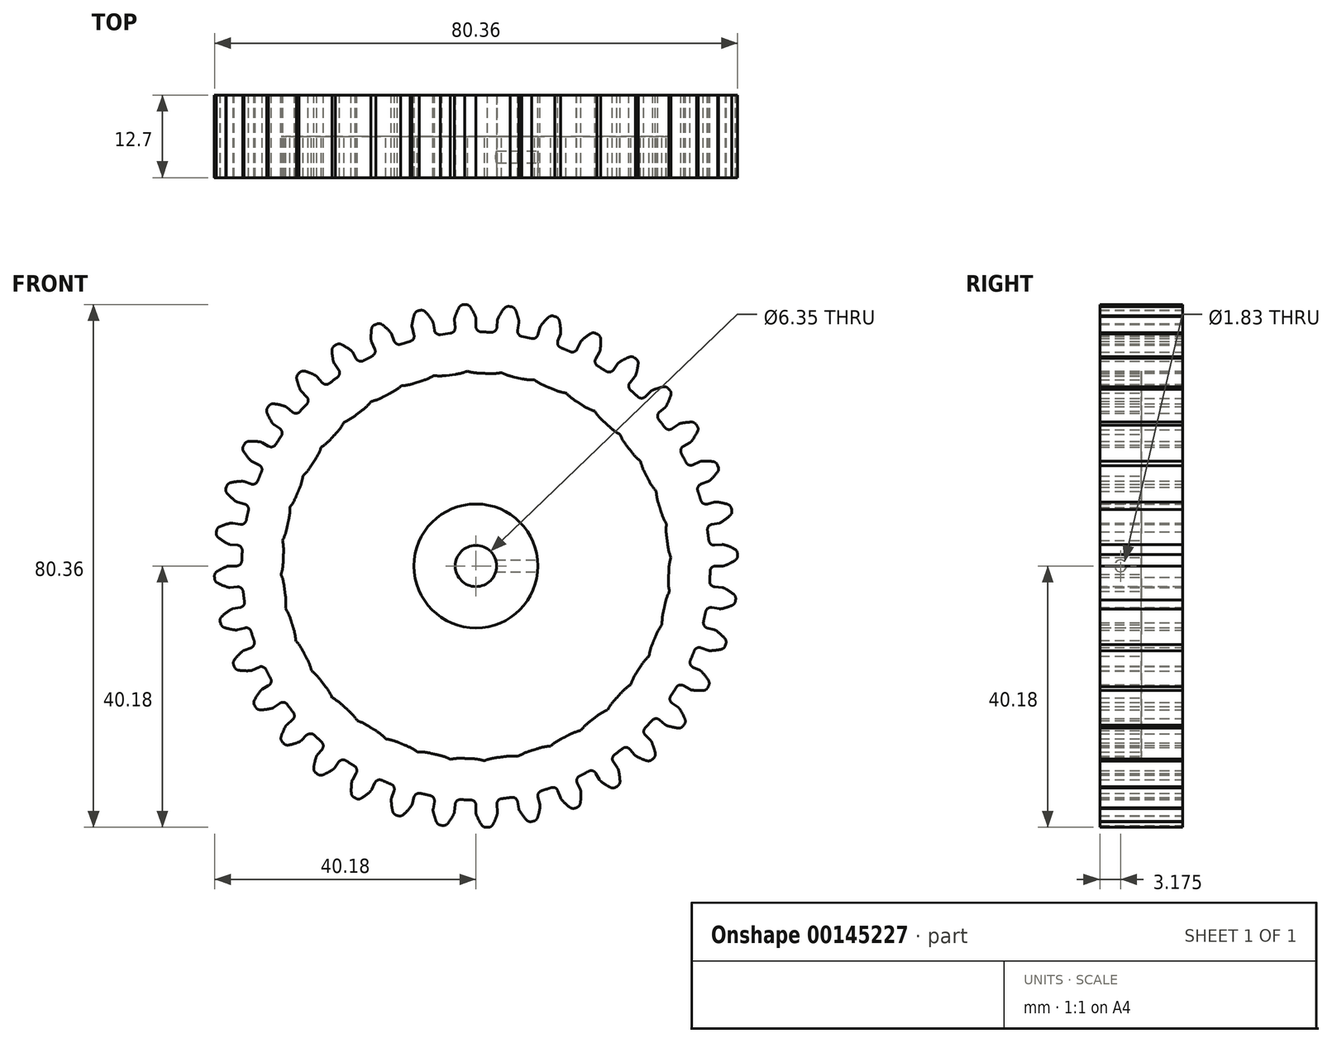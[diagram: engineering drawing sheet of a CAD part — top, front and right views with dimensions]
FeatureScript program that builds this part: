
annotation { "Feature Type Name" : "Feature", "Feature Type Description" : "" }
export const myFeature = defineFeature(function(context is Context, id is Id, definition is map)
    precondition{}
    {
        {
            var Q0;
            Q0=qCreatedBy(makeId("Front.planeOp"),FACE);
            var sketch = newSketch(context, id + "F0", { "sketchPlane" : qUnion([Q0])});
            skArc(sketch, "E0.trimOffspring", {"start": v(-8.9, 34.68) * mm, "mid": v(-8.89, 34.67) * mm, "end": v(-8.88, 34.67) * mm});
            skArc(sketch, "E1.trimOffspring", {"start": v(-0.06, 38.25) * mm, "mid": v(-0.43, 39.05) * mm, "end": v(-0.86, 39.8) * mm});
            skLineSegment(sketch, "E2", {"start": v(-1.59, 40.18) * mm, "end": v(-1.75, 40.18) * mm});
            skLineSegment(sketch, "E3", {"start": v(0, 37.94) * mm, "end": v(0, 36.8) * mm});
            skLineSegment(sketch, "E4.MirrorCS", {"start": v(-1.92, 40.17) * mm, "end": v(-1.75, 40.18) * mm});
            skArc(sketch, "E5.MirrorCS", {"start": v(-3.27, 38.11) * mm, "mid": v(-2.98, 38.94) * mm, "end": v(-2.6, 39.73) * mm});
            skLineSegment(sketch, "E6.MirrorCS", {"start": v(-3.3, 37.8) * mm, "end": v(-3.2, 36.66) * mm});
            skPoint(sketch, "E7.visualSharp", {"position": v(-3.14, 35.85) * mm});
            skArc(sketch, "E7.filletArc", {"start": v(-3.94, 35.77) * mm, "mid": v(-3.4, 36.06) * mm, "end": v(-3.2, 36.66) * mm});
            skPoint(sketch, "E8.visualSharp", {"position": v(0, 35.98) * mm});
            skArc(sketch, "E8.filletArc", {"start": v(0, 36.8) * mm, "mid": v(0.24, 36.22) * mm, "end": v(0.8, 35.97) * mm});
            skPoint(sketch, "E9.visualSharp", {"position": v(-3.32, 37.96) * mm});
            skArc(sketch, "E9.filletArc", {"start": v(-3.27, 38.11) * mm, "mid": v(-3.3, 37.96) * mm, "end": v(-3.3, 37.8) * mm});
            skArc(sketch, "E10.filletArc", {"start": v(0, 37.94) * mm, "mid": v(-0.02, 38.1) * mm, "end": v(-0.06, 38.25) * mm});
            skPoint(sketch, "E11.visualSharp", {"position": v(-2.38, 40.15) * mm});
            skArc(sketch, "E11.filletArc", {"start": v(-1.92, 40.17) * mm, "mid": v(-2.32, 40.04) * mm, "end": v(-2.6, 39.73) * mm});
            skPoint(sketch, "E12.visualSharp", {"position": v(-1.13, 40.2) * mm});
            skArc(sketch, "E12.filletArc", {"start": v(-0.86, 39.8) * mm, "mid": v(-1.18, 40.1) * mm, "end": v(-1.59, 40.18) * mm});
            skArc(sketch, "E13.1.0", {"start": v(-10.1, 34.54) * mm, "mid": v(-9.6, 34.93) * mm, "end": v(-9.52, 35.55) * mm});
            skLineSegment(sketch, "E13.1.1", {"start": v(-9.82, 36.65) * mm, "end": v(-9.52, 35.55) * mm});
            skArc(sketch, "E13.1.2", {"start": v(-9.84, 36.97) * mm, "mid": v(-9.7, 37.83) * mm, "end": v(-9.47, 38.67) * mm});
            skArc(sketch, "E13.1.3", {"start": v(-9.84, 36.97) * mm, "mid": v(-9.85, 36.8) * mm, "end": v(-9.82, 36.65) * mm});
            skArc(sketch, "E13.1.4", {"start": v(-8.87, 39.23) * mm, "mid": v(-9.24, 39.03) * mm, "end": v(-9.47, 38.67) * mm});
            skLineSegment(sketch, "E13.1.5", {"start": v(-8.87, 39.23) * mm, "end": v(-8.7, 39.26) * mm});
            skLineSegment(sketch, "E13.1.6", {"start": v(-8.54, 39.3) * mm, "end": v(-8.7, 39.26) * mm});
            skArc(sketch, "E13.1.7", {"start": v(-7.76, 39.05) * mm, "mid": v(-8.12, 39.28) * mm, "end": v(-8.54, 39.3) * mm});
            skArc(sketch, "E13.1.8", {"start": v(-6.7, 37.66) * mm, "mid": v(-7.2, 38.38) * mm, "end": v(-7.76, 39.05) * mm});
            skArc(sketch, "E13.1.9", {"start": v(-6.59, 37.37) * mm, "mid": v(-6.63, 37.52) * mm, "end": v(-6.7, 37.66) * mm});
            skLineSegment(sketch, "E13.1.10", {"start": v(-6.59, 37.37) * mm, "end": v(-6.4, 36.24) * mm});
            skArc(sketch, "E13.1.11", {"start": v(-6.4, 36.24) * mm, "mid": v(-6.06, 35.71) * mm, "end": v(-5.45, 35.57) * mm});
            skArc(sketch, "E13.2.0", {"start": v(-15.93, 32.26) * mm, "mid": v(-15.52, 32.73) * mm, "end": v(-15.55, 33.35) * mm});
            skLineSegment(sketch, "E13.2.1", {"start": v(-16.04, 34.39) * mm, "end": v(-15.55, 33.35) * mm});
            skArc(sketch, "E13.2.2", {"start": v(-16.11, 34.7) * mm, "mid": v(-16.12, 35.57) * mm, "end": v(-16.04, 36.44) * mm});
            skArc(sketch, "E13.2.3", {"start": v(-16.11, 34.7) * mm, "mid": v(-16.09, 34.54) * mm, "end": v(-16.04, 34.39) * mm});
            skArc(sketch, "E13.2.4", {"start": v(-15.54, 37.1) * mm, "mid": v(-15.88, 36.83) * mm, "end": v(-16.04, 36.44) * mm});
            skLineSegment(sketch, "E13.2.5", {"start": v(-15.54, 37.1) * mm, "end": v(-15.4, 37.16) * mm});
            skLineSegment(sketch, "E13.2.6", {"start": v(-15.24, 37.22) * mm, "end": v(-15.4, 37.16) * mm});
            skArc(sketch, "E13.2.7", {"start": v(-14.43, 37.1) * mm, "mid": v(-14.82, 37.27) * mm, "end": v(-15.24, 37.22) * mm});
            skArc(sketch, "E13.2.8", {"start": v(-13.14, 35.93) * mm, "mid": v(-13.76, 36.55) * mm, "end": v(-14.43, 37.1) * mm});
            skArc(sketch, "E13.2.9", {"start": v(-12.98, 35.65) * mm, "mid": v(-13.05, 35.8) * mm, "end": v(-13.14, 35.93) * mm});
            skLineSegment(sketch, "E13.2.10", {"start": v(-12.98, 35.65) * mm, "end": v(-12.59, 34.58) * mm});
            skArc(sketch, "E13.2.11", {"start": v(-12.59, 34.58) * mm, "mid": v(-12.17, 34.12) * mm, "end": v(-11.55, 34.08) * mm});
            skArc(sketch, "E13.3.0", {"start": v(-21.3, 29) * mm, "mid": v(-20.97, 29.54) * mm, "end": v(-21.1, 30.14) * mm});
            skLineSegment(sketch, "E13.3.1", {"start": v(-21.76, 31.08) * mm, "end": v(-21.1, 30.14) * mm});
            skArc(sketch, "E13.3.2", {"start": v(-21.9, 31.37) * mm, "mid": v(-22.05, 32.23) * mm, "end": v(-22.12, 33.1) * mm});
            skArc(sketch, "E13.3.3", {"start": v(-21.9, 31.37) * mm, "mid": v(-21.84, 31.22) * mm, "end": v(-21.76, 31.08) * mm});
            skArc(sketch, "E13.3.4", {"start": v(-21.75, 33.83) * mm, "mid": v(-22.03, 33.51) * mm, "end": v(-22.12, 33.1) * mm});
            skLineSegment(sketch, "E13.3.5", {"start": v(-21.75, 33.83) * mm, "end": v(-21.6, 33.92) * mm});
            skLineSegment(sketch, "E13.3.6", {"start": v(-21.47, 34) * mm, "end": v(-21.6, 33.92) * mm});
            skArc(sketch, "E13.3.7", {"start": v(-20.65, 34.04) * mm, "mid": v(-21.06, 34.13) * mm, "end": v(-21.47, 34) * mm});
            skArc(sketch, "E13.3.8", {"start": v(-19.18, 33.1) * mm, "mid": v(-19.9, 33.6) * mm, "end": v(-20.65, 34.04) * mm});
            skArc(sketch, "E13.3.9", {"start": v(-18.97, 32.86) * mm, "mid": v(-19.06, 32.99) * mm, "end": v(-19.18, 33.1) * mm});
            skLineSegment(sketch, "E13.3.10", {"start": v(-18.97, 32.86) * mm, "end": v(-18.4, 31.87) * mm});
            skArc(sketch, "E13.3.11", {"start": v(-18.4, 31.87) * mm, "mid": v(-17.9, 31.49) * mm, "end": v(-17.29, 31.56) * mm});
            skArc(sketch, "E13.4.0", {"start": v(-26, 24.87) * mm, "mid": v(-25.78, 25.45) * mm, "end": v(-26.02, 26.02) * mm});
            skLineSegment(sketch, "E13.4.1", {"start": v(-26.83, 26.83) * mm, "end": v(-26.02, 26.02) * mm});
            skArc(sketch, "E13.4.2", {"start": v(-27, 27.1) * mm, "mid": v(-27.3, 27.91) * mm, "end": v(-27.53, 28.76) * mm});
            skArc(sketch, "E13.4.3", {"start": v(-27, 27.1) * mm, "mid": v(-26.93, 26.95) * mm, "end": v(-26.83, 26.83) * mm});
            skArc(sketch, "E13.4.4", {"start": v(-27.3, 29.54) * mm, "mid": v(-27.52, 29.18) * mm, "end": v(-27.53, 28.76) * mm});
            skLineSegment(sketch, "E13.4.5", {"start": v(-27.3, 29.54) * mm, "end": v(-27.17, 29.65) * mm});
            skLineSegment(sketch, "E13.4.6", {"start": v(-27.05, 29.76) * mm, "end": v(-27.17, 29.65) * mm});
            skArc(sketch, "E13.4.7", {"start": v(-26.25, 29.94) * mm, "mid": v(-26.67, 29.95) * mm, "end": v(-27.05, 29.76) * mm});
            skArc(sketch, "E13.4.8", {"start": v(-24.64, 29.26) * mm, "mid": v(-25.43, 29.64) * mm, "end": v(-26.25, 29.94) * mm});
            skArc(sketch, "E13.4.9", {"start": v(-24.39, 29.07) * mm, "mid": v(-24.5, 29.18) * mm, "end": v(-24.64, 29.26) * mm});
            skLineSegment(sketch, "E13.4.10", {"start": v(-24.39, 29.07) * mm, "end": v(-23.65, 28.19) * mm});
            skArc(sketch, "E13.4.11", {"start": v(-23.65, 28.19) * mm, "mid": v(-23.1, 27.9) * mm, "end": v(-22.5, 28.08) * mm});
            skArc(sketch, "E13.5.0", {"start": v(-29.93, 19.97) * mm, "mid": v(-29.8, 20.58) * mm, "end": v(-30.14, 21.1) * mm});
            skLineSegment(sketch, "E13.5.1", {"start": v(-31.08, 21.76) * mm, "end": v(-30.14, 21.1) * mm});
            skArc(sketch, "E13.5.2", {"start": v(-31.3, 22) * mm, "mid": v(-31.74, 22.75) * mm, "end": v(-32.11, 23.54) * mm});
            skArc(sketch, "E13.5.3", {"start": v(-31.3, 22) * mm, "mid": v(-31.2, 21.87) * mm, "end": v(-31.08, 21.76) * mm});
            skArc(sketch, "E13.5.4", {"start": v(-32, 24.35) * mm, "mid": v(-32.17, 23.96) * mm, "end": v(-32.11, 23.54) * mm});
            skLineSegment(sketch, "E13.5.5", {"start": v(-32, 24.35) * mm, "end": v(-31.9, 24.48) * mm});
            skLineSegment(sketch, "E13.5.6", {"start": v(-31.8, 24.61) * mm, "end": v(-31.9, 24.48) * mm});
            skArc(sketch, "E13.5.7", {"start": v(-31.05, 24.92) * mm, "mid": v(-31.47, 24.87) * mm, "end": v(-31.8, 24.61) * mm});
            skArc(sketch, "E13.5.8", {"start": v(-29.34, 24.54) * mm, "mid": v(-30.19, 24.77) * mm, "end": v(-31.05, 24.92) * mm});
            skArc(sketch, "E13.5.9", {"start": v(-29.07, 24.39) * mm, "mid": v(-29.2, 24.48) * mm, "end": v(-29.34, 24.54) * mm});
            skLineSegment(sketch, "E13.5.10", {"start": v(-29.07, 24.39) * mm, "end": v(-28.19, 23.65) * mm});
            skArc(sketch, "E13.5.11", {"start": v(-28.19, 23.65) * mm, "mid": v(-27.6, 23.46) * mm, "end": v(-27.04, 23.74) * mm});
            skArc(sketch, "E13.6.0", {"start": v(-32.94, 14.47) * mm, "mid": v(-32.93, 15.1) * mm, "end": v(-33.35, 15.55) * mm});
            skLineSegment(sketch, "E13.6.1", {"start": v(-34.39, 16.04) * mm, "end": v(-33.35, 15.55) * mm});
            skArc(sketch, "E13.6.2", {"start": v(-34.64, 16.22) * mm, "mid": v(-35.2, 16.89) * mm, "end": v(-35.7, 17.6) * mm});
            skArc(sketch, "E13.6.3", {"start": v(-34.64, 16.22) * mm, "mid": v(-34.52, 16.12) * mm, "end": v(-34.39, 16.04) * mm});
            skArc(sketch, "E13.6.4", {"start": v(-35.75, 18.42) * mm, "mid": v(-35.84, 18) * mm, "end": v(-35.7, 17.6) * mm});
            skLineSegment(sketch, "E13.6.5", {"start": v(-35.75, 18.42) * mm, "end": v(-35.67, 18.57) * mm});
            skLineSegment(sketch, "E13.6.6", {"start": v(-35.6, 18.72) * mm, "end": v(-35.67, 18.57) * mm});
            skArc(sketch, "E13.6.7", {"start": v(-34.9, 19.15) * mm, "mid": v(-35.3, 19.03) * mm, "end": v(-35.6, 18.72) * mm});
            skArc(sketch, "E13.6.8", {"start": v(-33.16, 19.07) * mm, "mid": v(-34.03, 19.15) * mm, "end": v(-34.9, 19.15) * mm});
            skArc(sketch, "E13.6.9", {"start": v(-32.86, 18.97) * mm, "mid": v(-33, 19.04) * mm, "end": v(-33.16, 19.07) * mm});
            skLineSegment(sketch, "E13.6.10", {"start": v(-32.86, 18.97) * mm, "end": v(-31.87, 18.4) * mm});
            skArc(sketch, "E13.6.11", {"start": v(-31.87, 18.4) * mm, "mid": v(-31.25, 18.31) * mm, "end": v(-30.75, 18.69) * mm});
            skArc(sketch, "E13.7.0", {"start": v(-34.96, 8.53) * mm, "mid": v(-35.05, 9.15) * mm, "end": v(-35.55, 9.52) * mm});
            skLineSegment(sketch, "E13.7.1", {"start": v(-36.65, 9.82) * mm, "end": v(-35.55, 9.52) * mm});
            skArc(sketch, "E13.7.2", {"start": v(-36.93, 9.96) * mm, "mid": v(-37.6, 10.52) * mm, "end": v(-38.22, 11.14) * mm});
            skArc(sketch, "E13.7.3", {"start": v(-36.93, 9.96) * mm, "mid": v(-36.8, 9.88) * mm, "end": v(-36.65, 9.82) * mm});
            skArc(sketch, "E13.7.4", {"start": v(-38.4, 11.94) * mm, "mid": v(-38.42, 11.51) * mm, "end": v(-38.22, 11.14) * mm});
            skLineSegment(sketch, "E13.7.5", {"start": v(-38.4, 11.94) * mm, "end": v(-38.36, 12.1) * mm});
            skLineSegment(sketch, "E13.7.6", {"start": v(-38.3, 12.25) * mm, "end": v(-38.36, 12.1) * mm});
            skArc(sketch, "E13.7.7", {"start": v(-37.7, 12.8) * mm, "mid": v(-38.08, 12.6) * mm, "end": v(-38.3, 12.25) * mm});
            skArc(sketch, "E13.7.8", {"start": v(-35.97, 13.03) * mm, "mid": v(-36.84, 12.95) * mm, "end": v(-37.7, 12.8) * mm});
            skArc(sketch, "E13.7.9", {"start": v(-35.65, 12.98) * mm, "mid": v(-35.8, 13.02) * mm, "end": v(-35.97, 13.03) * mm});
            skLineSegment(sketch, "E13.7.10", {"start": v(-35.65, 12.98) * mm, "end": v(-34.58, 12.59) * mm});
            skArc(sketch, "E13.7.11", {"start": v(-34.58, 12.59) * mm, "mid": v(-33.96, 12.6) * mm, "end": v(-33.53, 13.06) * mm});
            skArc(sketch, "E13.8.0", {"start": v(-35.9, 2.33) * mm, "mid": v(-36.1, 2.92) * mm, "end": v(-36.66, 3.2) * mm});
            skLineSegment(sketch, "E13.8.1", {"start": v(-37.8, 3.3) * mm, "end": v(-36.66, 3.2) * mm});
            skArc(sketch, "E13.8.2", {"start": v(-38.1, 3.4) * mm, "mid": v(-38.86, 3.83) * mm, "end": v(-39.58, 4.33) * mm});
            skArc(sketch, "E13.8.3", {"start": v(-38.1, 3.4) * mm, "mid": v(-37.95, 3.34) * mm, "end": v(-37.8, 3.3) * mm});
            skArc(sketch, "E13.8.4", {"start": v(-39.9, 5.09) * mm, "mid": v(-39.84, 4.67) * mm, "end": v(-39.58, 4.33) * mm});
            skLineSegment(sketch, "E13.8.5", {"start": v(-39.9, 5.09) * mm, "end": v(-39.87, 5.25) * mm});
            skLineSegment(sketch, "E13.8.6", {"start": v(-39.85, 5.41) * mm, "end": v(-39.87, 5.25) * mm});
            skArc(sketch, "E13.8.7", {"start": v(-39.35, 6.06) * mm, "mid": v(-39.69, 5.8) * mm, "end": v(-39.85, 5.41) * mm});
            skArc(sketch, "E13.8.8", {"start": v(-37.68, 6.58) * mm, "mid": v(-38.53, 6.36) * mm, "end": v(-39.35, 6.06) * mm});
            skArc(sketch, "E13.8.9", {"start": v(-37.37, 6.59) * mm, "mid": v(-37.52, 6.6) * mm, "end": v(-37.68, 6.58) * mm});
            skLineSegment(sketch, "E13.8.10", {"start": v(-37.37, 6.59) * mm, "end": v(-36.24, 6.4) * mm});
            skArc(sketch, "E13.8.11", {"start": v(-36.24, 6.4) * mm, "mid": v(-35.63, 6.52) * mm, "end": v(-35.29, 7.04) * mm});
            skArc(sketch, "E13.9.0", {"start": v(-35.77, -3.94) * mm, "mid": v(-36.06, -3.4) * mm, "end": v(-36.66, -3.2) * mm});
            skLineSegment(sketch, "E13.9.1", {"start": v(-37.8, -3.3) * mm, "end": v(-36.66, -3.2) * mm});
            skArc(sketch, "E13.9.2", {"start": v(-38.11, -3.27) * mm, "mid": v(-38.94, -2.98) * mm, "end": v(-39.73, -2.6) * mm});
            skArc(sketch, "E13.9.3", {"start": v(-38.11, -3.27) * mm, "mid": v(-37.96, -3.3) * mm, "end": v(-37.8, -3.3) * mm});
            skArc(sketch, "E13.9.4", {"start": v(-40.17, -1.92) * mm, "mid": v(-40.04, -2.32) * mm, "end": v(-39.73, -2.6) * mm});
            skLineSegment(sketch, "E13.9.5", {"start": v(-40.17, -1.92) * mm, "end": v(-40.18, -1.75) * mm});
            skLineSegment(sketch, "E13.9.6", {"start": v(-40.18, -1.59) * mm, "end": v(-40.18, -1.75) * mm});
            skArc(sketch, "E13.9.7", {"start": v(-39.8, -0.86) * mm, "mid": v(-40.1, -1.18) * mm, "end": v(-40.18, -1.59) * mm});
            skArc(sketch, "E13.9.8", {"start": v(-38.25, -0.06) * mm, "mid": v(-39.05, -0.43) * mm, "end": v(-39.8, -0.86) * mm});
            skArc(sketch, "E13.9.9", {"start": v(-37.94, 0) * mm, "mid": v(-38.1, -0.02) * mm, "end": v(-38.25, -0.06) * mm});
            skLineSegment(sketch, "E13.9.10", {"start": v(-37.94, 0) * mm, "end": v(-36.8, 0) * mm});
            skArc(sketch, "E13.9.11", {"start": v(-36.8, 0) * mm, "mid": v(-36.22, 0.24) * mm, "end": v(-35.97, 0.8) * mm});
            skArc(sketch, "E13.10.0", {"start": v(-34.54, -10.1) * mm, "mid": v(-34.93, -9.6) * mm, "end": v(-35.55, -9.52) * mm});
            skLineSegment(sketch, "E13.10.1", {"start": v(-36.65, -9.82) * mm, "end": v(-35.55, -9.52) * mm});
            skArc(sketch, "E13.10.2", {"start": v(-36.97, -9.84) * mm, "mid": v(-37.83, -9.7) * mm, "end": v(-38.67, -9.47) * mm});
            skArc(sketch, "E13.10.3", {"start": v(-36.97, -9.84) * mm, "mid": v(-36.8, -9.85) * mm, "end": v(-36.65, -9.82) * mm});
            skArc(sketch, "E13.10.4", {"start": v(-39.23, -8.87) * mm, "mid": v(-39.03, -9.24) * mm, "end": v(-38.67, -9.47) * mm});
            skLineSegment(sketch, "E13.10.5", {"start": v(-39.23, -8.87) * mm, "end": v(-39.26, -8.7) * mm});
            skLineSegment(sketch, "E13.10.6", {"start": v(-39.3, -8.54) * mm, "end": v(-39.26, -8.7) * mm});
            skArc(sketch, "E13.10.7", {"start": v(-39.05, -7.76) * mm, "mid": v(-39.28, -8.12) * mm, "end": v(-39.3, -8.54) * mm});
            skArc(sketch, "E13.10.8", {"start": v(-37.66, -6.7) * mm, "mid": v(-38.38, -7.2) * mm, "end": v(-39.05, -7.76) * mm});
            skArc(sketch, "E13.10.9", {"start": v(-37.37, -6.59) * mm, "mid": v(-37.52, -6.63) * mm, "end": v(-37.66, -6.7) * mm});
            skLineSegment(sketch, "E13.10.10", {"start": v(-37.37, -6.59) * mm, "end": v(-36.24, -6.4) * mm});
            skArc(sketch, "E13.10.11", {"start": v(-36.24, -6.4) * mm, "mid": v(-35.71, -6.06) * mm, "end": v(-35.57, -5.45) * mm});
            skArc(sketch, "E13.11.0", {"start": v(-32.26, -15.93) * mm, "mid": v(-32.73, -15.52) * mm, "end": v(-33.35, -15.55) * mm});
            skLineSegment(sketch, "E13.11.1", {"start": v(-34.39, -16.04) * mm, "end": v(-33.35, -15.55) * mm});
            skArc(sketch, "E13.11.2", {"start": v(-34.7, -16.11) * mm, "mid": v(-35.57, -16.12) * mm, "end": v(-36.44, -16.04) * mm});
            skArc(sketch, "E13.11.3", {"start": v(-34.7, -16.11) * mm, "mid": v(-34.54, -16.09) * mm, "end": v(-34.39, -16.04) * mm});
            skArc(sketch, "E13.11.4", {"start": v(-37.1, -15.54) * mm, "mid": v(-36.83, -15.88) * mm, "end": v(-36.44, -16.04) * mm});
            skLineSegment(sketch, "E13.11.5", {"start": v(-37.1, -15.54) * mm, "end": v(-37.16, -15.4) * mm});
            skLineSegment(sketch, "E13.11.6", {"start": v(-37.22, -15.24) * mm, "end": v(-37.16, -15.4) * mm});
            skArc(sketch, "E13.11.7", {"start": v(-37.1, -14.43) * mm, "mid": v(-37.27, -14.82) * mm, "end": v(-37.22, -15.24) * mm});
            skArc(sketch, "E13.11.8", {"start": v(-35.93, -13.14) * mm, "mid": v(-36.55, -13.76) * mm, "end": v(-37.1, -14.43) * mm});
            skArc(sketch, "E13.11.9", {"start": v(-35.65, -12.98) * mm, "mid": v(-35.8, -13.05) * mm, "end": v(-35.93, -13.14) * mm});
            skLineSegment(sketch, "E13.11.10", {"start": v(-35.65, -12.98) * mm, "end": v(-34.58, -12.59) * mm});
            skArc(sketch, "E13.11.11", {"start": v(-34.58, -12.59) * mm, "mid": v(-34.12, -12.17) * mm, "end": v(-34.08, -11.55) * mm});
            skArc(sketch, "E13.12.0", {"start": v(-29, -21.3) * mm, "mid": v(-29.54, -20.97) * mm, "end": v(-30.14, -21.1) * mm});
            skLineSegment(sketch, "E13.12.1", {"start": v(-31.08, -21.76) * mm, "end": v(-30.14, -21.1) * mm});
            skArc(sketch, "E13.12.2", {"start": v(-31.37, -21.9) * mm, "mid": v(-32.23, -22.05) * mm, "end": v(-33.1, -22.12) * mm});
            skArc(sketch, "E13.12.3", {"start": v(-31.37, -21.9) * mm, "mid": v(-31.22, -21.84) * mm, "end": v(-31.08, -21.76) * mm});
            skArc(sketch, "E13.12.4", {"start": v(-33.83, -21.75) * mm, "mid": v(-33.51, -22.03) * mm, "end": v(-33.1, -22.12) * mm});
            skLineSegment(sketch, "E13.12.5", {"start": v(-33.83, -21.75) * mm, "end": v(-33.92, -21.6) * mm});
            skLineSegment(sketch, "E13.12.6", {"start": v(-34, -21.47) * mm, "end": v(-33.92, -21.6) * mm});
            skArc(sketch, "E13.12.7", {"start": v(-34.04, -20.65) * mm, "mid": v(-34.13, -21.06) * mm, "end": v(-34, -21.47) * mm});
            skArc(sketch, "E13.12.8", {"start": v(-33.1, -19.18) * mm, "mid": v(-33.6, -19.9) * mm, "end": v(-34.04, -20.65) * mm});
            skArc(sketch, "E13.12.9", {"start": v(-32.86, -18.97) * mm, "mid": v(-32.99, -19.06) * mm, "end": v(-33.1, -19.18) * mm});
            skLineSegment(sketch, "E13.12.10", {"start": v(-32.86, -18.97) * mm, "end": v(-31.87, -18.4) * mm});
            skArc(sketch, "E13.12.11", {"start": v(-31.87, -18.4) * mm, "mid": v(-31.49, -17.9) * mm, "end": v(-31.56, -17.29) * mm});
            skArc(sketch, "E13.13.0", {"start": v(-24.87, -26) * mm, "mid": v(-25.45, -25.78) * mm, "end": v(-26.02, -26.02) * mm});
            skLineSegment(sketch, "E13.13.1", {"start": v(-26.83, -26.83) * mm, "end": v(-26.02, -26.02) * mm});
            skArc(sketch, "E13.13.2", {"start": v(-27.1, -27) * mm, "mid": v(-27.91, -27.3) * mm, "end": v(-28.76, -27.53) * mm});
            skArc(sketch, "E13.13.3", {"start": v(-27.1, -27) * mm, "mid": v(-26.95, -26.93) * mm, "end": v(-26.83, -26.83) * mm});
            skArc(sketch, "E13.13.4", {"start": v(-29.54, -27.3) * mm, "mid": v(-29.18, -27.52) * mm, "end": v(-28.76, -27.53) * mm});
            skLineSegment(sketch, "E13.13.5", {"start": v(-29.54, -27.3) * mm, "end": v(-29.65, -27.17) * mm});
            skLineSegment(sketch, "E13.13.6", {"start": v(-29.76, -27.05) * mm, "end": v(-29.65, -27.17) * mm});
            skArc(sketch, "E13.13.7", {"start": v(-29.94, -26.25) * mm, "mid": v(-29.95, -26.67) * mm, "end": v(-29.76, -27.05) * mm});
            skArc(sketch, "E13.13.8", {"start": v(-29.26, -24.64) * mm, "mid": v(-29.64, -25.43) * mm, "end": v(-29.94, -26.25) * mm});
            skArc(sketch, "E13.13.9", {"start": v(-29.07, -24.39) * mm, "mid": v(-29.18, -24.5) * mm, "end": v(-29.26, -24.64) * mm});
            skLineSegment(sketch, "E13.13.10", {"start": v(-29.07, -24.39) * mm, "end": v(-28.19, -23.65) * mm});
            skArc(sketch, "E13.13.11", {"start": v(-28.19, -23.65) * mm, "mid": v(-27.9, -23.1) * mm, "end": v(-28.08, -22.5) * mm});
            skArc(sketch, "E13.14.0", {"start": v(-19.97, -29.93) * mm, "mid": v(-20.58, -29.8) * mm, "end": v(-21.1, -30.14) * mm});
            skLineSegment(sketch, "E13.14.1", {"start": v(-21.76, -31.08) * mm, "end": v(-21.1, -30.14) * mm});
            skArc(sketch, "E13.14.2", {"start": v(-22, -31.3) * mm, "mid": v(-22.75, -31.74) * mm, "end": v(-23.54, -32.11) * mm});
            skArc(sketch, "E13.14.3", {"start": v(-22, -31.3) * mm, "mid": v(-21.87, -31.2) * mm, "end": v(-21.76, -31.08) * mm});
            skArc(sketch, "E13.14.4", {"start": v(-24.35, -32) * mm, "mid": v(-23.96, -32.17) * mm, "end": v(-23.54, -32.11) * mm});
            skLineSegment(sketch, "E13.14.5", {"start": v(-24.35, -32) * mm, "end": v(-24.48, -31.9) * mm});
            skLineSegment(sketch, "E13.14.6", {"start": v(-24.61, -31.8) * mm, "end": v(-24.48, -31.9) * mm});
            skArc(sketch, "E13.14.7", {"start": v(-24.92, -31.05) * mm, "mid": v(-24.87, -31.47) * mm, "end": v(-24.61, -31.8) * mm});
            skArc(sketch, "E13.14.8", {"start": v(-24.54, -29.34) * mm, "mid": v(-24.77, -30.19) * mm, "end": v(-24.92, -31.05) * mm});
            skArc(sketch, "E13.14.9", {"start": v(-24.39, -29.07) * mm, "mid": v(-24.48, -29.2) * mm, "end": v(-24.54, -29.34) * mm});
            skLineSegment(sketch, "E13.14.10", {"start": v(-24.39, -29.07) * mm, "end": v(-23.65, -28.19) * mm});
            skArc(sketch, "E13.14.11", {"start": v(-23.65, -28.19) * mm, "mid": v(-23.46, -27.6) * mm, "end": v(-23.74, -27.04) * mm});
            skArc(sketch, "E13.15.0", {"start": v(-14.47, -32.94) * mm, "mid": v(-15.1, -32.93) * mm, "end": v(-15.55, -33.35) * mm});
            skLineSegment(sketch, "E13.15.1", {"start": v(-16.04, -34.39) * mm, "end": v(-15.55, -33.35) * mm});
            skArc(sketch, "E13.15.2", {"start": v(-16.22, -34.64) * mm, "mid": v(-16.89, -35.2) * mm, "end": v(-17.6, -35.7) * mm});
            skArc(sketch, "E13.15.3", {"start": v(-16.22, -34.64) * mm, "mid": v(-16.12, -34.52) * mm, "end": v(-16.04, -34.39) * mm});
            skArc(sketch, "E13.15.4", {"start": v(-18.42, -35.75) * mm, "mid": v(-18, -35.84) * mm, "end": v(-17.6, -35.7) * mm});
            skLineSegment(sketch, "E13.15.5", {"start": v(-18.42, -35.75) * mm, "end": v(-18.57, -35.67) * mm});
            skLineSegment(sketch, "E13.15.6", {"start": v(-18.72, -35.6) * mm, "end": v(-18.57, -35.67) * mm});
            skArc(sketch, "E13.15.7", {"start": v(-19.15, -34.9) * mm, "mid": v(-19.03, -35.3) * mm, "end": v(-18.72, -35.6) * mm});
            skArc(sketch, "E13.15.8", {"start": v(-19.07, -33.16) * mm, "mid": v(-19.15, -34.03) * mm, "end": v(-19.15, -34.9) * mm});
            skArc(sketch, "E13.15.9", {"start": v(-18.97, -32.86) * mm, "mid": v(-19.04, -33) * mm, "end": v(-19.07, -33.16) * mm});
            skLineSegment(sketch, "E13.15.10", {"start": v(-18.97, -32.86) * mm, "end": v(-18.4, -31.87) * mm});
            skArc(sketch, "E13.15.11", {"start": v(-18.4, -31.87) * mm, "mid": v(-18.31, -31.25) * mm, "end": v(-18.69, -30.75) * mm});
            skArc(sketch, "E13.16.0", {"start": v(-8.53, -34.96) * mm, "mid": v(-9.15, -35.05) * mm, "end": v(-9.52, -35.55) * mm});
            skLineSegment(sketch, "E13.16.1", {"start": v(-9.82, -36.65) * mm, "end": v(-9.52, -35.55) * mm});
            skArc(sketch, "E13.16.2", {"start": v(-9.96, -36.93) * mm, "mid": v(-10.52, -37.6) * mm, "end": v(-11.14, -38.22) * mm});
            skArc(sketch, "E13.16.3", {"start": v(-9.96, -36.93) * mm, "mid": v(-9.88, -36.8) * mm, "end": v(-9.82, -36.65) * mm});
            skArc(sketch, "E13.16.4", {"start": v(-11.94, -38.4) * mm, "mid": v(-11.51, -38.42) * mm, "end": v(-11.14, -38.22) * mm});
            skLineSegment(sketch, "E13.16.5", {"start": v(-11.94, -38.4) * mm, "end": v(-12.1, -38.36) * mm});
            skLineSegment(sketch, "E13.16.6", {"start": v(-12.25, -38.3) * mm, "end": v(-12.1, -38.36) * mm});
            skArc(sketch, "E13.16.7", {"start": v(-12.8, -37.7) * mm, "mid": v(-12.6, -38.08) * mm, "end": v(-12.25, -38.3) * mm});
            skArc(sketch, "E13.16.8", {"start": v(-13.03, -35.97) * mm, "mid": v(-12.95, -36.84) * mm, "end": v(-12.8, -37.7) * mm});
            skArc(sketch, "E13.16.9", {"start": v(-12.98, -35.65) * mm, "mid": v(-13.02, -35.8) * mm, "end": v(-13.03, -35.97) * mm});
            skLineSegment(sketch, "E13.16.10", {"start": v(-12.98, -35.65) * mm, "end": v(-12.59, -34.58) * mm});
            skArc(sketch, "E13.16.11", {"start": v(-12.59, -34.58) * mm, "mid": v(-12.6, -33.96) * mm, "end": v(-13.06, -33.53) * mm});
            skArc(sketch, "E13.17.0", {"start": v(-2.33, -35.9) * mm, "mid": v(-2.92, -36.1) * mm, "end": v(-3.2, -36.66) * mm});
            skLineSegment(sketch, "E13.17.1", {"start": v(-3.3, -37.8) * mm, "end": v(-3.2, -36.66) * mm});
            skArc(sketch, "E13.17.2", {"start": v(-3.4, -38.1) * mm, "mid": v(-3.83, -38.86) * mm, "end": v(-4.33, -39.58) * mm});
            skArc(sketch, "E13.17.3", {"start": v(-3.4, -38.1) * mm, "mid": v(-3.34, -37.95) * mm, "end": v(-3.3, -37.8) * mm});
            skArc(sketch, "E13.17.4", {"start": v(-5.09, -39.9) * mm, "mid": v(-4.67, -39.84) * mm, "end": v(-4.33, -39.58) * mm});
            skLineSegment(sketch, "E13.17.5", {"start": v(-5.09, -39.9) * mm, "end": v(-5.25, -39.87) * mm});
            skLineSegment(sketch, "E13.17.6", {"start": v(-5.41, -39.85) * mm, "end": v(-5.25, -39.87) * mm});
            skArc(sketch, "E13.17.7", {"start": v(-6.06, -39.35) * mm, "mid": v(-5.8, -39.69) * mm, "end": v(-5.41, -39.85) * mm});
            skArc(sketch, "E13.17.8", {"start": v(-6.58, -37.68) * mm, "mid": v(-6.36, -38.53) * mm, "end": v(-6.06, -39.35) * mm});
            skArc(sketch, "E13.17.9", {"start": v(-6.59, -37.37) * mm, "mid": v(-6.6, -37.52) * mm, "end": v(-6.58, -37.68) * mm});
            skLineSegment(sketch, "E13.17.10", {"start": v(-6.59, -37.37) * mm, "end": v(-6.4, -36.24) * mm});
            skArc(sketch, "E13.17.11", {"start": v(-6.4, -36.24) * mm, "mid": v(-6.52, -35.63) * mm, "end": v(-7.04, -35.29) * mm});
            skArc(sketch, "E13.18.0", {"start": v(3.94, -35.77) * mm, "mid": v(3.4, -36.06) * mm, "end": v(3.2, -36.66) * mm});
            skLineSegment(sketch, "E13.18.1", {"start": v(3.3, -37.8) * mm, "end": v(3.2, -36.66) * mm});
            skArc(sketch, "E13.18.2", {"start": v(3.27, -38.11) * mm, "mid": v(2.98, -38.94) * mm, "end": v(2.6, -39.73) * mm});
            skArc(sketch, "E13.18.3", {"start": v(3.27, -38.11) * mm, "mid": v(3.3, -37.96) * mm, "end": v(3.3, -37.8) * mm});
            skArc(sketch, "E13.18.4", {"start": v(1.92, -40.17) * mm, "mid": v(2.32, -40.04) * mm, "end": v(2.6, -39.73) * mm});
            skLineSegment(sketch, "E13.18.5", {"start": v(1.92, -40.17) * mm, "end": v(1.75, -40.18) * mm});
            skLineSegment(sketch, "E13.18.6", {"start": v(1.59, -40.18) * mm, "end": v(1.75, -40.18) * mm});
            skArc(sketch, "E13.18.7", {"start": v(0.86, -39.8) * mm, "mid": v(1.18, -40.1) * mm, "end": v(1.59, -40.18) * mm});
            skArc(sketch, "E13.18.8", {"start": v(0.06, -38.25) * mm, "mid": v(0.43, -39.05) * mm, "end": v(0.86, -39.8) * mm});
            skArc(sketch, "E13.18.9", {"start": v(0, -37.94) * mm, "mid": v(0.02, -38.1) * mm, "end": v(0.06, -38.25) * mm});
            skLineSegment(sketch, "E13.18.10", {"start": v(0, -37.94) * mm, "end": v(0, -36.8) * mm});
            skArc(sketch, "E13.18.11", {"start": v(0, -36.8) * mm, "mid": v(-0.24, -36.22) * mm, "end": v(-0.8, -35.97) * mm});
            skArc(sketch, "E13.19.0", {"start": v(10.1, -34.54) * mm, "mid": v(9.6, -34.93) * mm, "end": v(9.52, -35.55) * mm});
            skLineSegment(sketch, "E13.19.1", {"start": v(9.82, -36.65) * mm, "end": v(9.52, -35.55) * mm});
            skArc(sketch, "E13.19.2", {"start": v(9.84, -36.97) * mm, "mid": v(9.7, -37.83) * mm, "end": v(9.47, -38.67) * mm});
            skArc(sketch, "E13.19.3", {"start": v(9.84, -36.97) * mm, "mid": v(9.85, -36.8) * mm, "end": v(9.82, -36.65) * mm});
            skArc(sketch, "E13.19.4", {"start": v(8.87, -39.23) * mm, "mid": v(9.24, -39.03) * mm, "end": v(9.47, -38.67) * mm});
            skLineSegment(sketch, "E13.19.5", {"start": v(8.87, -39.23) * mm, "end": v(8.7, -39.26) * mm});
            skLineSegment(sketch, "E13.19.6", {"start": v(8.54, -39.3) * mm, "end": v(8.7, -39.26) * mm});
            skArc(sketch, "E13.19.7", {"start": v(7.76, -39.05) * mm, "mid": v(8.12, -39.28) * mm, "end": v(8.54, -39.3) * mm});
            skArc(sketch, "E13.19.8", {"start": v(6.7, -37.66) * mm, "mid": v(7.2, -38.38) * mm, "end": v(7.76, -39.05) * mm});
            skArc(sketch, "E13.19.9", {"start": v(6.59, -37.37) * mm, "mid": v(6.63, -37.52) * mm, "end": v(6.7, -37.66) * mm});
            skLineSegment(sketch, "E13.19.10", {"start": v(6.59, -37.37) * mm, "end": v(6.4, -36.24) * mm});
            skArc(sketch, "E13.19.11", {"start": v(6.4, -36.24) * mm, "mid": v(6.06, -35.71) * mm, "end": v(5.45, -35.57) * mm});
            skArc(sketch, "E13.20.0", {"start": v(15.93, -32.26) * mm, "mid": v(15.52, -32.73) * mm, "end": v(15.55, -33.35) * mm});
            skLineSegment(sketch, "E13.20.1", {"start": v(16.04, -34.39) * mm, "end": v(15.55, -33.35) * mm});
            skArc(sketch, "E13.20.2", {"start": v(16.11, -34.7) * mm, "mid": v(16.12, -35.57) * mm, "end": v(16.04, -36.44) * mm});
            skArc(sketch, "E13.20.3", {"start": v(16.11, -34.7) * mm, "mid": v(16.09, -34.54) * mm, "end": v(16.04, -34.39) * mm});
            skArc(sketch, "E13.20.4", {"start": v(15.54, -37.1) * mm, "mid": v(15.88, -36.83) * mm, "end": v(16.04, -36.44) * mm});
            skLineSegment(sketch, "E13.20.5", {"start": v(15.54, -37.1) * mm, "end": v(15.4, -37.16) * mm});
            skLineSegment(sketch, "E13.20.6", {"start": v(15.24, -37.22) * mm, "end": v(15.4, -37.16) * mm});
            skArc(sketch, "E13.20.7", {"start": v(14.43, -37.1) * mm, "mid": v(14.82, -37.27) * mm, "end": v(15.24, -37.22) * mm});
            skArc(sketch, "E13.20.8", {"start": v(13.14, -35.93) * mm, "mid": v(13.76, -36.55) * mm, "end": v(14.43, -37.1) * mm});
            skArc(sketch, "E13.20.9", {"start": v(12.98, -35.65) * mm, "mid": v(13.05, -35.8) * mm, "end": v(13.14, -35.93) * mm});
            skLineSegment(sketch, "E13.20.10", {"start": v(12.98, -35.65) * mm, "end": v(12.59, -34.58) * mm});
            skArc(sketch, "E13.20.11", {"start": v(12.59, -34.58) * mm, "mid": v(12.17, -34.12) * mm, "end": v(11.55, -34.08) * mm});
            skArc(sketch, "E13.21.0", {"start": v(21.3, -29) * mm, "mid": v(20.97, -29.54) * mm, "end": v(21.1, -30.14) * mm});
            skLineSegment(sketch, "E13.21.1", {"start": v(21.76, -31.08) * mm, "end": v(21.1, -30.14) * mm});
            skArc(sketch, "E13.21.2", {"start": v(21.9, -31.37) * mm, "mid": v(22.05, -32.23) * mm, "end": v(22.12, -33.1) * mm});
            skArc(sketch, "E13.21.3", {"start": v(21.9, -31.37) * mm, "mid": v(21.84, -31.22) * mm, "end": v(21.76, -31.08) * mm});
            skArc(sketch, "E13.21.4", {"start": v(21.75, -33.83) * mm, "mid": v(22.03, -33.51) * mm, "end": v(22.12, -33.1) * mm});
            skLineSegment(sketch, "E13.21.5", {"start": v(21.75, -33.83) * mm, "end": v(21.6, -33.92) * mm});
            skLineSegment(sketch, "E13.21.6", {"start": v(21.47, -34) * mm, "end": v(21.6, -33.92) * mm});
            skArc(sketch, "E13.21.7", {"start": v(20.65, -34.04) * mm, "mid": v(21.06, -34.13) * mm, "end": v(21.47, -34) * mm});
            skArc(sketch, "E13.21.8", {"start": v(19.18, -33.1) * mm, "mid": v(19.9, -33.6) * mm, "end": v(20.65, -34.04) * mm});
            skArc(sketch, "E13.21.9", {"start": v(18.97, -32.86) * mm, "mid": v(19.06, -32.99) * mm, "end": v(19.18, -33.1) * mm});
            skLineSegment(sketch, "E13.21.10", {"start": v(18.97, -32.86) * mm, "end": v(18.4, -31.87) * mm});
            skArc(sketch, "E13.21.11", {"start": v(18.4, -31.87) * mm, "mid": v(17.9, -31.49) * mm, "end": v(17.29, -31.56) * mm});
            skArc(sketch, "E13.22.0", {"start": v(26, -24.87) * mm, "mid": v(25.78, -25.45) * mm, "end": v(26.02, -26.02) * mm});
            skLineSegment(sketch, "E13.22.1", {"start": v(26.83, -26.83) * mm, "end": v(26.02, -26.02) * mm});
            skArc(sketch, "E13.22.2", {"start": v(27, -27.1) * mm, "mid": v(27.3, -27.91) * mm, "end": v(27.53, -28.76) * mm});
            skArc(sketch, "E13.22.3", {"start": v(27, -27.1) * mm, "mid": v(26.93, -26.95) * mm, "end": v(26.83, -26.83) * mm});
            skArc(sketch, "E13.22.4", {"start": v(27.3, -29.54) * mm, "mid": v(27.52, -29.18) * mm, "end": v(27.53, -28.76) * mm});
            skLineSegment(sketch, "E13.22.5", {"start": v(27.3, -29.54) * mm, "end": v(27.17, -29.65) * mm});
            skLineSegment(sketch, "E13.22.6", {"start": v(27.05, -29.76) * mm, "end": v(27.17, -29.65) * mm});
            skArc(sketch, "E13.22.7", {"start": v(26.25, -29.94) * mm, "mid": v(26.67, -29.95) * mm, "end": v(27.05, -29.76) * mm});
            skArc(sketch, "E13.22.8", {"start": v(24.64, -29.26) * mm, "mid": v(25.43, -29.64) * mm, "end": v(26.25, -29.94) * mm});
            skArc(sketch, "E13.22.9", {"start": v(24.39, -29.07) * mm, "mid": v(24.5, -29.18) * mm, "end": v(24.64, -29.26) * mm});
            skLineSegment(sketch, "E13.22.10", {"start": v(24.39, -29.07) * mm, "end": v(23.65, -28.19) * mm});
            skArc(sketch, "E13.22.11", {"start": v(23.65, -28.19) * mm, "mid": v(23.1, -27.9) * mm, "end": v(22.5, -28.08) * mm});
            skArc(sketch, "E13.23.0", {"start": v(29.93, -19.97) * mm, "mid": v(29.8, -20.58) * mm, "end": v(30.14, -21.1) * mm});
            skLineSegment(sketch, "E13.23.1", {"start": v(31.08, -21.76) * mm, "end": v(30.14, -21.1) * mm});
            skArc(sketch, "E13.23.2", {"start": v(31.3, -22) * mm, "mid": v(31.74, -22.75) * mm, "end": v(32.11, -23.54) * mm});
            skArc(sketch, "E13.23.3", {"start": v(31.3, -22) * mm, "mid": v(31.2, -21.87) * mm, "end": v(31.08, -21.76) * mm});
            skArc(sketch, "E13.23.4", {"start": v(32, -24.35) * mm, "mid": v(32.17, -23.96) * mm, "end": v(32.11, -23.54) * mm});
            skLineSegment(sketch, "E13.23.5", {"start": v(32, -24.35) * mm, "end": v(31.9, -24.48) * mm});
            skLineSegment(sketch, "E13.23.6", {"start": v(31.8, -24.61) * mm, "end": v(31.9, -24.48) * mm});
            skArc(sketch, "E13.23.7", {"start": v(31.05, -24.92) * mm, "mid": v(31.47, -24.87) * mm, "end": v(31.8, -24.61) * mm});
            skArc(sketch, "E13.23.8", {"start": v(29.34, -24.54) * mm, "mid": v(30.19, -24.77) * mm, "end": v(31.05, -24.92) * mm});
            skArc(sketch, "E13.23.9", {"start": v(29.07, -24.39) * mm, "mid": v(29.2, -24.48) * mm, "end": v(29.34, -24.54) * mm});
            skLineSegment(sketch, "E13.23.10", {"start": v(29.07, -24.39) * mm, "end": v(28.19, -23.65) * mm});
            skArc(sketch, "E13.23.11", {"start": v(28.19, -23.65) * mm, "mid": v(27.6, -23.46) * mm, "end": v(27.04, -23.74) * mm});
            skArc(sketch, "E13.24.0", {"start": v(32.94, -14.47) * mm, "mid": v(32.93, -15.1) * mm, "end": v(33.35, -15.55) * mm});
            skLineSegment(sketch, "E13.24.1", {"start": v(34.39, -16.04) * mm, "end": v(33.35, -15.55) * mm});
            skArc(sketch, "E13.24.2", {"start": v(34.64, -16.22) * mm, "mid": v(35.2, -16.89) * mm, "end": v(35.7, -17.6) * mm});
            skArc(sketch, "E13.24.3", {"start": v(34.64, -16.22) * mm, "mid": v(34.52, -16.12) * mm, "end": v(34.39, -16.04) * mm});
            skArc(sketch, "E13.24.4", {"start": v(35.75, -18.42) * mm, "mid": v(35.84, -18) * mm, "end": v(35.7, -17.6) * mm});
            skLineSegment(sketch, "E13.24.5", {"start": v(35.75, -18.42) * mm, "end": v(35.67, -18.57) * mm});
            skLineSegment(sketch, "E13.24.6", {"start": v(35.6, -18.72) * mm, "end": v(35.67, -18.57) * mm});
            skArc(sketch, "E13.24.7", {"start": v(34.9, -19.15) * mm, "mid": v(35.3, -19.03) * mm, "end": v(35.6, -18.72) * mm});
            skArc(sketch, "E13.24.8", {"start": v(33.16, -19.07) * mm, "mid": v(34.03, -19.15) * mm, "end": v(34.9, -19.15) * mm});
            skArc(sketch, "E13.24.9", {"start": v(32.86, -18.97) * mm, "mid": v(33, -19.04) * mm, "end": v(33.16, -19.07) * mm});
            skLineSegment(sketch, "E13.24.10", {"start": v(32.86, -18.97) * mm, "end": v(31.87, -18.4) * mm});
            skArc(sketch, "E13.24.11", {"start": v(31.87, -18.4) * mm, "mid": v(31.25, -18.31) * mm, "end": v(30.75, -18.69) * mm});
            skArc(sketch, "E13.25.0", {"start": v(34.96, -8.53) * mm, "mid": v(35.05, -9.15) * mm, "end": v(35.55, -9.52) * mm});
            skLineSegment(sketch, "E13.25.1", {"start": v(36.65, -9.82) * mm, "end": v(35.55, -9.52) * mm});
            skArc(sketch, "E13.25.2", {"start": v(36.93, -9.96) * mm, "mid": v(37.6, -10.52) * mm, "end": v(38.22, -11.14) * mm});
            skArc(sketch, "E13.25.3", {"start": v(36.93, -9.96) * mm, "mid": v(36.8, -9.88) * mm, "end": v(36.65, -9.82) * mm});
            skArc(sketch, "E13.25.4", {"start": v(38.4, -11.94) * mm, "mid": v(38.42, -11.51) * mm, "end": v(38.22, -11.14) * mm});
            skLineSegment(sketch, "E13.25.5", {"start": v(38.4, -11.94) * mm, "end": v(38.36, -12.1) * mm});
            skLineSegment(sketch, "E13.25.6", {"start": v(38.3, -12.25) * mm, "end": v(38.36, -12.1) * mm});
            skArc(sketch, "E13.25.7", {"start": v(37.7, -12.8) * mm, "mid": v(38.08, -12.6) * mm, "end": v(38.3, -12.25) * mm});
            skArc(sketch, "E13.25.8", {"start": v(35.97, -13.03) * mm, "mid": v(36.84, -12.95) * mm, "end": v(37.7, -12.8) * mm});
            skArc(sketch, "E13.25.9", {"start": v(35.65, -12.98) * mm, "mid": v(35.8, -13.02) * mm, "end": v(35.97, -13.03) * mm});
            skLineSegment(sketch, "E13.25.10", {"start": v(35.65, -12.98) * mm, "end": v(34.58, -12.59) * mm});
            skArc(sketch, "E13.25.11", {"start": v(34.58, -12.59) * mm, "mid": v(33.96, -12.6) * mm, "end": v(33.53, -13.06) * mm});
            skArc(sketch, "E13.26.0", {"start": v(35.9, -2.33) * mm, "mid": v(36.1, -2.92) * mm, "end": v(36.66, -3.2) * mm});
            skLineSegment(sketch, "E13.26.1", {"start": v(37.8, -3.3) * mm, "end": v(36.66, -3.2) * mm});
            skArc(sketch, "E13.26.2", {"start": v(38.1, -3.4) * mm, "mid": v(38.86, -3.83) * mm, "end": v(39.58, -4.33) * mm});
            skArc(sketch, "E13.26.3", {"start": v(38.1, -3.4) * mm, "mid": v(37.95, -3.34) * mm, "end": v(37.8, -3.3) * mm});
            skArc(sketch, "E13.26.4", {"start": v(39.9, -5.09) * mm, "mid": v(39.84, -4.67) * mm, "end": v(39.58, -4.33) * mm});
            skLineSegment(sketch, "E13.26.5", {"start": v(39.9, -5.09) * mm, "end": v(39.87, -5.25) * mm});
            skLineSegment(sketch, "E13.26.6", {"start": v(39.85, -5.41) * mm, "end": v(39.87, -5.25) * mm});
            skArc(sketch, "E13.26.7", {"start": v(39.35, -6.06) * mm, "mid": v(39.69, -5.8) * mm, "end": v(39.85, -5.41) * mm});
            skArc(sketch, "E13.26.8", {"start": v(37.68, -6.58) * mm, "mid": v(38.53, -6.36) * mm, "end": v(39.35, -6.06) * mm});
            skArc(sketch, "E13.26.9", {"start": v(37.37, -6.59) * mm, "mid": v(37.52, -6.6) * mm, "end": v(37.68, -6.58) * mm});
            skLineSegment(sketch, "E13.26.10", {"start": v(37.37, -6.59) * mm, "end": v(36.24, -6.4) * mm});
            skArc(sketch, "E13.26.11", {"start": v(36.24, -6.4) * mm, "mid": v(35.63, -6.52) * mm, "end": v(35.29, -7.04) * mm});
            skArc(sketch, "E13.27.0", {"start": v(35.77, 3.94) * mm, "mid": v(36.06, 3.4) * mm, "end": v(36.66, 3.2) * mm});
            skLineSegment(sketch, "E13.27.1", {"start": v(37.8, 3.3) * mm, "end": v(36.66, 3.2) * mm});
            skArc(sketch, "E13.27.2", {"start": v(38.11, 3.27) * mm, "mid": v(38.94, 2.98) * mm, "end": v(39.73, 2.6) * mm});
            skArc(sketch, "E13.27.3", {"start": v(38.11, 3.27) * mm, "mid": v(37.96, 3.3) * mm, "end": v(37.8, 3.3) * mm});
            skArc(sketch, "E13.27.4", {"start": v(40.17, 1.92) * mm, "mid": v(40.04, 2.32) * mm, "end": v(39.73, 2.6) * mm});
            skLineSegment(sketch, "E13.27.5", {"start": v(40.17, 1.92) * mm, "end": v(40.18, 1.75) * mm});
            skLineSegment(sketch, "E13.27.6", {"start": v(40.18, 1.59) * mm, "end": v(40.18, 1.75) * mm});
            skArc(sketch, "E13.27.7", {"start": v(39.8, 0.86) * mm, "mid": v(40.1, 1.18) * mm, "end": v(40.18, 1.59) * mm});
            skArc(sketch, "E13.27.8", {"start": v(38.25, 0.06) * mm, "mid": v(39.05, 0.43) * mm, "end": v(39.8, 0.86) * mm});
            skArc(sketch, "E13.27.9", {"start": v(37.94, 0) * mm, "mid": v(38.1, 0.02) * mm, "end": v(38.25, 0.06) * mm});
            skLineSegment(sketch, "E13.27.10", {"start": v(37.94, 0) * mm, "end": v(36.8, 0) * mm});
            skArc(sketch, "E13.27.11", {"start": v(36.8, 0) * mm, "mid": v(36.22, -0.24) * mm, "end": v(35.97, -0.8) * mm});
            skArc(sketch, "E13.28.0", {"start": v(34.54, 10.1) * mm, "mid": v(34.93, 9.6) * mm, "end": v(35.55, 9.52) * mm});
            skLineSegment(sketch, "E13.28.1", {"start": v(36.65, 9.82) * mm, "end": v(35.55, 9.52) * mm});
            skArc(sketch, "E13.28.2", {"start": v(36.97, 9.84) * mm, "mid": v(37.83, 9.7) * mm, "end": v(38.67, 9.47) * mm});
            skArc(sketch, "E13.28.3", {"start": v(36.97, 9.84) * mm, "mid": v(36.8, 9.85) * mm, "end": v(36.65, 9.82) * mm});
            skArc(sketch, "E13.28.4", {"start": v(39.23, 8.87) * mm, "mid": v(39.03, 9.24) * mm, "end": v(38.67, 9.47) * mm});
            skLineSegment(sketch, "E13.28.5", {"start": v(39.23, 8.87) * mm, "end": v(39.26, 8.7) * mm});
            skLineSegment(sketch, "E13.28.6", {"start": v(39.3, 8.54) * mm, "end": v(39.26, 8.7) * mm});
            skArc(sketch, "E13.28.7", {"start": v(39.05, 7.76) * mm, "mid": v(39.28, 8.12) * mm, "end": v(39.3, 8.54) * mm});
            skArc(sketch, "E13.28.8", {"start": v(37.66, 6.7) * mm, "mid": v(38.38, 7.2) * mm, "end": v(39.05, 7.76) * mm});
            skArc(sketch, "E13.28.9", {"start": v(37.37, 6.59) * mm, "mid": v(37.52, 6.63) * mm, "end": v(37.66, 6.7) * mm});
            skLineSegment(sketch, "E13.28.10", {"start": v(37.37, 6.59) * mm, "end": v(36.24, 6.4) * mm});
            skArc(sketch, "E13.28.11", {"start": v(36.24, 6.4) * mm, "mid": v(35.71, 6.06) * mm, "end": v(35.57, 5.45) * mm});
            skArc(sketch, "E13.29.0", {"start": v(32.26, 15.93) * mm, "mid": v(32.73, 15.52) * mm, "end": v(33.35, 15.55) * mm});
            skLineSegment(sketch, "E13.29.1", {"start": v(34.39, 16.04) * mm, "end": v(33.35, 15.55) * mm});
            skArc(sketch, "E13.29.2", {"start": v(34.7, 16.11) * mm, "mid": v(35.57, 16.12) * mm, "end": v(36.44, 16.04) * mm});
            skArc(sketch, "E13.29.3", {"start": v(34.7, 16.11) * mm, "mid": v(34.54, 16.09) * mm, "end": v(34.39, 16.04) * mm});
            skArc(sketch, "E13.29.4", {"start": v(37.1, 15.54) * mm, "mid": v(36.83, 15.88) * mm, "end": v(36.44, 16.04) * mm});
            skLineSegment(sketch, "E13.29.5", {"start": v(37.1, 15.54) * mm, "end": v(37.16, 15.4) * mm});
            skLineSegment(sketch, "E13.29.6", {"start": v(37.22, 15.24) * mm, "end": v(37.16, 15.4) * mm});
            skArc(sketch, "E13.29.7", {"start": v(37.1, 14.43) * mm, "mid": v(37.27, 14.82) * mm, "end": v(37.22, 15.24) * mm});
            skArc(sketch, "E13.29.8", {"start": v(35.93, 13.14) * mm, "mid": v(36.55, 13.76) * mm, "end": v(37.1, 14.43) * mm});
            skArc(sketch, "E13.29.9", {"start": v(35.65, 12.98) * mm, "mid": v(35.8, 13.05) * mm, "end": v(35.93, 13.14) * mm});
            skLineSegment(sketch, "E13.29.10", {"start": v(35.65, 12.98) * mm, "end": v(34.58, 12.59) * mm});
            skArc(sketch, "E13.29.11", {"start": v(34.58, 12.59) * mm, "mid": v(34.12, 12.17) * mm, "end": v(34.08, 11.55) * mm});
            skArc(sketch, "E13.30.0", {"start": v(29, 21.3) * mm, "mid": v(29.54, 20.97) * mm, "end": v(30.14, 21.1) * mm});
            skLineSegment(sketch, "E13.30.1", {"start": v(31.08, 21.76) * mm, "end": v(30.14, 21.1) * mm});
            skArc(sketch, "E13.30.2", {"start": v(31.37, 21.9) * mm, "mid": v(32.23, 22.05) * mm, "end": v(33.1, 22.12) * mm});
            skArc(sketch, "E13.30.3", {"start": v(31.37, 21.9) * mm, "mid": v(31.22, 21.84) * mm, "end": v(31.08, 21.76) * mm});
            skArc(sketch, "E13.30.4", {"start": v(33.83, 21.75) * mm, "mid": v(33.51, 22.03) * mm, "end": v(33.1, 22.12) * mm});
            skLineSegment(sketch, "E13.30.5", {"start": v(33.83, 21.75) * mm, "end": v(33.92, 21.6) * mm});
            skLineSegment(sketch, "E13.30.6", {"start": v(34, 21.47) * mm, "end": v(33.92, 21.6) * mm});
            skArc(sketch, "E13.30.7", {"start": v(34.04, 20.65) * mm, "mid": v(34.13, 21.06) * mm, "end": v(34, 21.47) * mm});
            skArc(sketch, "E13.30.8", {"start": v(33.1, 19.18) * mm, "mid": v(33.6, 19.9) * mm, "end": v(34.04, 20.65) * mm});
            skArc(sketch, "E13.30.9", {"start": v(32.86, 18.97) * mm, "mid": v(32.99, 19.06) * mm, "end": v(33.1, 19.18) * mm});
            skLineSegment(sketch, "E13.30.10", {"start": v(32.86, 18.97) * mm, "end": v(31.87, 18.4) * mm});
            skArc(sketch, "E13.30.11", {"start": v(31.87, 18.4) * mm, "mid": v(31.49, 17.9) * mm, "end": v(31.56, 17.29) * mm});
            skArc(sketch, "E13.31.0", {"start": v(24.87, 26) * mm, "mid": v(25.45, 25.78) * mm, "end": v(26.02, 26.02) * mm});
            skLineSegment(sketch, "E13.31.1", {"start": v(26.83, 26.83) * mm, "end": v(26.02, 26.02) * mm});
            skArc(sketch, "E13.31.2", {"start": v(27.1, 27) * mm, "mid": v(27.91, 27.3) * mm, "end": v(28.76, 27.53) * mm});
            skArc(sketch, "E13.31.3", {"start": v(27.1, 27) * mm, "mid": v(26.95, 26.93) * mm, "end": v(26.83, 26.83) * mm});
            skArc(sketch, "E13.31.4", {"start": v(29.54, 27.3) * mm, "mid": v(29.18, 27.52) * mm, "end": v(28.76, 27.53) * mm});
            skLineSegment(sketch, "E13.31.5", {"start": v(29.54, 27.3) * mm, "end": v(29.65, 27.17) * mm});
            skLineSegment(sketch, "E13.31.6", {"start": v(29.76, 27.05) * mm, "end": v(29.65, 27.17) * mm});
            skArc(sketch, "E13.31.7", {"start": v(29.94, 26.25) * mm, "mid": v(29.95, 26.67) * mm, "end": v(29.76, 27.05) * mm});
            skArc(sketch, "E13.31.8", {"start": v(29.26, 24.64) * mm, "mid": v(29.64, 25.43) * mm, "end": v(29.94, 26.25) * mm});
            skArc(sketch, "E13.31.9", {"start": v(29.07, 24.39) * mm, "mid": v(29.18, 24.5) * mm, "end": v(29.26, 24.64) * mm});
            skLineSegment(sketch, "E13.31.10", {"start": v(29.07, 24.39) * mm, "end": v(28.19, 23.65) * mm});
            skArc(sketch, "E13.31.11", {"start": v(28.19, 23.65) * mm, "mid": v(27.9, 23.1) * mm, "end": v(28.08, 22.5) * mm});
            skArc(sketch, "E13.32.0", {"start": v(19.97, 29.93) * mm, "mid": v(20.58, 29.8) * mm, "end": v(21.1, 30.14) * mm});
            skLineSegment(sketch, "E13.32.1", {"start": v(21.76, 31.08) * mm, "end": v(21.1, 30.14) * mm});
            skArc(sketch, "E13.32.2", {"start": v(22, 31.3) * mm, "mid": v(22.75, 31.74) * mm, "end": v(23.54, 32.11) * mm});
            skArc(sketch, "E13.32.3", {"start": v(22, 31.3) * mm, "mid": v(21.87, 31.2) * mm, "end": v(21.76, 31.08) * mm});
            skArc(sketch, "E13.32.4", {"start": v(24.35, 32) * mm, "mid": v(23.96, 32.17) * mm, "end": v(23.54, 32.11) * mm});
            skLineSegment(sketch, "E13.32.5", {"start": v(24.35, 32) * mm, "end": v(24.48, 31.9) * mm});
            skLineSegment(sketch, "E13.32.6", {"start": v(24.61, 31.8) * mm, "end": v(24.48, 31.9) * mm});
            skArc(sketch, "E13.32.7", {"start": v(24.92, 31.05) * mm, "mid": v(24.87, 31.47) * mm, "end": v(24.61, 31.8) * mm});
            skArc(sketch, "E13.32.8", {"start": v(24.54, 29.34) * mm, "mid": v(24.77, 30.19) * mm, "end": v(24.92, 31.05) * mm});
            skArc(sketch, "E13.32.9", {"start": v(24.39, 29.07) * mm, "mid": v(24.48, 29.2) * mm, "end": v(24.54, 29.34) * mm});
            skLineSegment(sketch, "E13.32.10", {"start": v(24.39, 29.07) * mm, "end": v(23.65, 28.19) * mm});
            skArc(sketch, "E13.32.11", {"start": v(23.65, 28.19) * mm, "mid": v(23.46, 27.6) * mm, "end": v(23.74, 27.04) * mm});
            skArc(sketch, "E13.33.0", {"start": v(14.47, 32.94) * mm, "mid": v(15.1, 32.93) * mm, "end": v(15.55, 33.35) * mm});
            skLineSegment(sketch, "E13.33.1", {"start": v(16.04, 34.39) * mm, "end": v(15.55, 33.35) * mm});
            skArc(sketch, "E13.33.2", {"start": v(16.22, 34.64) * mm, "mid": v(16.89, 35.2) * mm, "end": v(17.6, 35.7) * mm});
            skArc(sketch, "E13.33.3", {"start": v(16.22, 34.64) * mm, "mid": v(16.12, 34.52) * mm, "end": v(16.04, 34.39) * mm});
            skArc(sketch, "E13.33.4", {"start": v(18.42, 35.75) * mm, "mid": v(18, 35.84) * mm, "end": v(17.6, 35.7) * mm});
            skLineSegment(sketch, "E13.33.5", {"start": v(18.42, 35.75) * mm, "end": v(18.57, 35.67) * mm});
            skLineSegment(sketch, "E13.33.6", {"start": v(18.72, 35.6) * mm, "end": v(18.57, 35.67) * mm});
            skArc(sketch, "E13.33.7", {"start": v(19.15, 34.9) * mm, "mid": v(19.03, 35.3) * mm, "end": v(18.72, 35.6) * mm});
            skArc(sketch, "E13.33.8", {"start": v(19.07, 33.16) * mm, "mid": v(19.15, 34.03) * mm, "end": v(19.15, 34.9) * mm});
            skArc(sketch, "E13.33.9", {"start": v(18.97, 32.86) * mm, "mid": v(19.04, 33) * mm, "end": v(19.07, 33.16) * mm});
            skLineSegment(sketch, "E13.33.10", {"start": v(18.97, 32.86) * mm, "end": v(18.4, 31.87) * mm});
            skArc(sketch, "E13.33.11", {"start": v(18.4, 31.87) * mm, "mid": v(18.31, 31.25) * mm, "end": v(18.69, 30.75) * mm});
            skArc(sketch, "E13.34.0", {"start": v(8.53, 34.96) * mm, "mid": v(9.15, 35.05) * mm, "end": v(9.52, 35.55) * mm});
            skLineSegment(sketch, "E13.34.1", {"start": v(9.82, 36.65) * mm, "end": v(9.52, 35.55) * mm});
            skArc(sketch, "E13.34.2", {"start": v(9.96, 36.93) * mm, "mid": v(10.52, 37.6) * mm, "end": v(11.14, 38.22) * mm});
            skArc(sketch, "E13.34.3", {"start": v(9.96, 36.93) * mm, "mid": v(9.88, 36.8) * mm, "end": v(9.82, 36.65) * mm});
            skArc(sketch, "E13.34.4", {"start": v(11.94, 38.4) * mm, "mid": v(11.51, 38.42) * mm, "end": v(11.14, 38.22) * mm});
            skLineSegment(sketch, "E13.34.5", {"start": v(11.94, 38.4) * mm, "end": v(12.1, 38.36) * mm});
            skLineSegment(sketch, "E13.34.6", {"start": v(12.25, 38.3) * mm, "end": v(12.1, 38.36) * mm});
            skArc(sketch, "E13.34.7", {"start": v(12.8, 37.7) * mm, "mid": v(12.6, 38.08) * mm, "end": v(12.25, 38.3) * mm});
            skArc(sketch, "E13.34.8", {"start": v(13.03, 35.97) * mm, "mid": v(12.95, 36.84) * mm, "end": v(12.8, 37.7) * mm});
            skArc(sketch, "E13.34.9", {"start": v(12.98, 35.65) * mm, "mid": v(13.02, 35.8) * mm, "end": v(13.03, 35.97) * mm});
            skLineSegment(sketch, "E13.34.10", {"start": v(12.98, 35.65) * mm, "end": v(12.59, 34.58) * mm});
            skArc(sketch, "E13.34.11", {"start": v(12.59, 34.58) * mm, "mid": v(12.6, 33.96) * mm, "end": v(13.06, 33.53) * mm});
            skArc(sketch, "E13.35.0", {"start": v(2.33, 35.9) * mm, "mid": v(2.92, 36.1) * mm, "end": v(3.2, 36.66) * mm});
            skLineSegment(sketch, "E13.35.1", {"start": v(3.3, 37.8) * mm, "end": v(3.2, 36.66) * mm});
            skArc(sketch, "E13.35.2", {"start": v(3.4, 38.1) * mm, "mid": v(3.83, 38.86) * mm, "end": v(4.33, 39.58) * mm});
            skArc(sketch, "E13.35.3", {"start": v(3.4, 38.1) * mm, "mid": v(3.34, 37.95) * mm, "end": v(3.3, 37.8) * mm});
            skArc(sketch, "E13.35.4", {"start": v(5.09, 39.9) * mm, "mid": v(4.67, 39.84) * mm, "end": v(4.33, 39.58) * mm});
            skLineSegment(sketch, "E13.35.5", {"start": v(5.09, 39.9) * mm, "end": v(5.25, 39.87) * mm});
            skLineSegment(sketch, "E13.35.6", {"start": v(5.41, 39.85) * mm, "end": v(5.25, 39.87) * mm});
            skArc(sketch, "E13.35.7", {"start": v(6.06, 39.35) * mm, "mid": v(5.8, 39.69) * mm, "end": v(5.41, 39.85) * mm});
            skArc(sketch, "E13.35.8", {"start": v(6.58, 37.68) * mm, "mid": v(6.36, 38.53) * mm, "end": v(6.06, 39.35) * mm});
            skArc(sketch, "E13.35.9", {"start": v(6.59, 37.37) * mm, "mid": v(6.6, 37.52) * mm, "end": v(6.58, 37.68) * mm});
            skLineSegment(sketch, "E13.35.10", {"start": v(6.59, 37.37) * mm, "end": v(6.4, 36.24) * mm});
            skArc(sketch, "E13.35.11", {"start": v(6.4, 36.24) * mm, "mid": v(6.52, 35.63) * mm, "end": v(7.04, 35.29) * mm});
            skPoint(sketch, "E13.center", {"position": v(0, 0) * mm});
            skArc(sketch, "E14.trimOffspring", {"start": v(14.47, 32.94) * mm, "mid": v(13.77, 33.24) * mm, "end": v(13.06, 33.53) * mm});
            skArc(sketch, "E15.trimOffspring", {"start": v(19.97, 29.93) * mm, "mid": v(19.33, 30.35) * mm, "end": v(18.69, 30.75) * mm});
            skArc(sketch, "E16.trimOffspring", {"start": v(24.87, 26) * mm, "mid": v(24.3, 26.53) * mm, "end": v(23.74, 27.04) * mm});
            skArc(sketch, "E17.trimOffspring", {"start": v(29, 21.3) * mm, "mid": v(28.55, 21.9) * mm, "end": v(28.08, 22.5) * mm});
            skArc(sketch, "E18.trimOffspring", {"start": v(32.26, 15.93) * mm, "mid": v(31.92, 16.62) * mm, "end": v(31.56, 17.29) * mm});
            skArc(sketch, "E19.trimOffspring", {"start": v(34.54, 10.1) * mm, "mid": v(34.32, 10.82) * mm, "end": v(34.08, 11.55) * mm});
            skArc(sketch, "E20.trimOffspring", {"start": v(35.77, 3.94) * mm, "mid": v(35.68, 4.7) * mm, "end": v(35.57, 5.45) * mm});
            skArc(sketch, "E21.trimOffspring", {"start": v(35.9, -2.33) * mm, "mid": v(35.95, -1.57) * mm, "end": v(35.97, -0.8) * mm});
            skArc(sketch, "E22.trimOffspring", {"start": v(34.96, -8.53) * mm, "mid": v(35.13, -7.79) * mm, "end": v(35.29, -7.04) * mm});
            skArc(sketch, "E23.trimOffspring", {"start": v(32.94, -14.47) * mm, "mid": v(33.24, -13.77) * mm, "end": v(33.53, -13.06) * mm});
            skArc(sketch, "E24.trimOffspring", {"start": v(29.93, -19.97) * mm, "mid": v(30.35, -19.33) * mm, "end": v(30.75, -18.69) * mm});
            skArc(sketch, "E25.trimOffspring", {"start": v(26, -24.87) * mm, "mid": v(26.53, -24.3) * mm, "end": v(27.04, -23.74) * mm});
            skArc(sketch, "E26.trimOffspring", {"start": v(21.3, -29) * mm, "mid": v(21.9, -28.55) * mm, "end": v(22.5, -28.08) * mm});
            skArc(sketch, "E27.trimOffspring", {"start": v(15.93, -32.26) * mm, "mid": v(16.62, -31.92) * mm, "end": v(17.29, -31.56) * mm});
            skArc(sketch, "E28.trimOffspring", {"start": v(10.1, -34.54) * mm, "mid": v(10.82, -34.32) * mm, "end": v(11.55, -34.08) * mm});
            skArc(sketch, "E29.trimOffspring", {"start": v(3.94, -35.77) * mm, "mid": v(4.7, -35.68) * mm, "end": v(5.45, -35.57) * mm});
            skArc(sketch, "E30.trimOffspring", {"start": v(-2.33, -35.9) * mm, "mid": v(-1.57, -35.95) * mm, "end": v(-0.8, -35.97) * mm});
            skArc(sketch, "E31.trimOffspring", {"start": v(-8.53, -34.96) * mm, "mid": v(-7.79, -35.13) * mm, "end": v(-7.04, -35.29) * mm});
            skArc(sketch, "E32.trimOffspring", {"start": v(-14.47, -32.94) * mm, "mid": v(-13.77, -33.24) * mm, "end": v(-13.06, -33.53) * mm});
            skArc(sketch, "E33.trimOffspring", {"start": v(-19.97, -29.93) * mm, "mid": v(-19.33, -30.35) * mm, "end": v(-18.69, -30.75) * mm});
            skArc(sketch, "E34.trimOffspring", {"start": v(-24.87, -26) * mm, "mid": v(-24.3, -26.53) * mm, "end": v(-23.74, -27.04) * mm});
            skArc(sketch, "E35.trimOffspring", {"start": v(-29, -21.3) * mm, "mid": v(-28.55, -21.9) * mm, "end": v(-28.08, -22.5) * mm});
            skArc(sketch, "E36.trimOffspring", {"start": v(-32.26, -15.93) * mm, "mid": v(-31.92, -16.62) * mm, "end": v(-31.56, -17.29) * mm});
            skArc(sketch, "E37.trimOffspring", {"start": v(-34.54, -10.1) * mm, "mid": v(-34.32, -10.82) * mm, "end": v(-34.08, -11.55) * mm});
            skArc(sketch, "E38.trimOffspring", {"start": v(-35.77, -3.94) * mm, "mid": v(-35.68, -4.7) * mm, "end": v(-35.57, -5.45) * mm});
            skArc(sketch, "E39.trimOffspring", {"start": v(-35.9, 2.33) * mm, "mid": v(-35.95, 1.57) * mm, "end": v(-35.97, 0.8) * mm});
            skArc(sketch, "E40.trimOffspring", {"start": v(-34.96, 8.53) * mm, "mid": v(-35.13, 7.79) * mm, "end": v(-35.29, 7.04) * mm});
            skArc(sketch, "E41.trimOffspring", {"start": v(-32.94, 14.47) * mm, "mid": v(-33.24, 13.77) * mm, "end": v(-33.53, 13.06) * mm});
            skArc(sketch, "E42.trimOffspring", {"start": v(-29.93, 19.97) * mm, "mid": v(-30.35, 19.33) * mm, "end": v(-30.75, 18.69) * mm});
            skArc(sketch, "E43.trimOffspring", {"start": v(-26, 24.87) * mm, "mid": v(-26.53, 24.3) * mm, "end": v(-27.04, 23.74) * mm});
            skArc(sketch, "E44.trimOffspring", {"start": v(-21.3, 29) * mm, "mid": v(-21.9, 28.55) * mm, "end": v(-22.5, 28.08) * mm});
            skArc(sketch, "E45.trimOffspring", {"start": v(-15.93, 32.26) * mm, "mid": v(-16.62, 31.92) * mm, "end": v(-17.29, 31.56) * mm});
            skArc(sketch, "E46.trimOffspring", {"start": v(2.33, 35.9) * mm, "mid": v(1.57, 35.95) * mm, "end": v(0.8, 35.97) * mm});
            skLineSegment(sketch, "E47", {"start": v(-11.55, 34.08) * mm, "end": v(-10.1, 34.54) * mm});
            skLineSegment(sketch, "E48", {"start": v(-5.45, 35.57) * mm, "end": v(-3.94, 35.77) * mm});
            skLineSegment(sketch, "E49", {"start": v(7.04, 35.29) * mm, "end": v(8.53, 34.96) * mm});
            skSolve(sketch);
        }
        {
            var Q0;
            Q0 = qSketchRegion(id + "F0", true);
            extrude(context, id + "F1", {"entities" : qUnion([Q0]), "depth" : 12.7 * mm});
        }
        {
            var Q0;
            Q0=makeQuery(id+"F1.opExtrude","CAP_FACE",FACE,{"disambiguationData":[OSD([sQuery(id+"F0.wireOp",EDGE,"E1.trimOffspring"),sQuery(id+"F0.wireOp",EDGE,"E2"),sQuery(id+"F0.wireOp",EDGE,"E3"),sQuery(id+"F0.wireOp",EDGE,"E4.MirrorCS"),sQuery(id+"F0.wireOp",EDGE,"E5.MirrorCS"),sQuery(id+"F0.wireOp",EDGE,"E6.MirrorCS"),sQuery(id+"F0.wireOp",EDGE,"E7.filletArc"),sQuery(id+"F0.wireOp",EDGE,"E8.filletArc"),sQuery(id+"F0.wireOp",EDGE,"E9.filletArc"),sQuery(id+"F0.wireOp",EDGE,"E10.filletArc"),sQuery(id+"F0.wireOp",EDGE,"E11.filletArc"),sQuery(id+"F0.wireOp",EDGE,"E12.filletArc"),sQuery(id+"F0.wireOp",EDGE,"E13.1.0"),sQuery(id+"F0.wireOp",EDGE,"E13.1.1"),sQuery(id+"F0.wireOp",EDGE,"E13.1.2"),sQuery(id+"F0.wireOp",EDGE,"E13.1.3"),sQuery(id+"F0.wireOp",EDGE,"E13.1.4"),sQuery(id+"F0.wireOp",EDGE,"E13.1.5"),sQuery(id+"F0.wireOp",EDGE,"E13.1.6"),sQuery(id+"F0.wireOp",EDGE,"E13.1.7"),sQuery(id+"F0.wireOp",EDGE,"E13.1.8"),sQuery(id+"F0.wireOp",EDGE,"E13.1.9"),sQuery(id+"F0.wireOp",EDGE,"E13.1.10"),sQuery(id+"F0.wireOp",EDGE,"E13.1.11"),sQuery(id+"F0.wireOp",EDGE,"E13.2.0"),sQuery(id+"F0.wireOp",EDGE,"E13.2.1"),sQuery(id+"F0.wireOp",EDGE,"E13.2.2"),sQuery(id+"F0.wireOp",EDGE,"E13.2.3"),sQuery(id+"F0.wireOp",EDGE,"E13.2.4"),sQuery(id+"F0.wireOp",EDGE,"E13.2.5"),sQuery(id+"F0.wireOp",EDGE,"E13.2.6"),sQuery(id+"F0.wireOp",EDGE,"E13.2.7"),sQuery(id+"F0.wireOp",EDGE,"E13.2.8"),sQuery(id+"F0.wireOp",EDGE,"E13.2.9"),sQuery(id+"F0.wireOp",EDGE,"E13.2.10"),sQuery(id+"F0.wireOp",EDGE,"E13.2.11"),sQuery(id+"F0.wireOp",EDGE,"E13.3.0"),sQuery(id+"F0.wireOp",EDGE,"E13.3.1"),sQuery(id+"F0.wireOp",EDGE,"E13.3.2"),sQuery(id+"F0.wireOp",EDGE,"E13.3.3"),sQuery(id+"F0.wireOp",EDGE,"E13.3.4"),sQuery(id+"F0.wireOp",EDGE,"E13.3.5"),sQuery(id+"F0.wireOp",EDGE,"E13.3.6"),sQuery(id+"F0.wireOp",EDGE,"E13.3.7"),sQuery(id+"F0.wireOp",EDGE,"E13.3.8"),sQuery(id+"F0.wireOp",EDGE,"E13.3.9"),sQuery(id+"F0.wireOp",EDGE,"E13.3.10"),sQuery(id+"F0.wireOp",EDGE,"E13.3.11"),sQuery(id+"F0.wireOp",EDGE,"E13.4.0"),sQuery(id+"F0.wireOp",EDGE,"E13.4.1"),sQuery(id+"F0.wireOp",EDGE,"E13.4.2"),sQuery(id+"F0.wireOp",EDGE,"E13.4.3"),sQuery(id+"F0.wireOp",EDGE,"E13.4.4"),sQuery(id+"F0.wireOp",EDGE,"E13.4.5"),sQuery(id+"F0.wireOp",EDGE,"E13.4.6"),sQuery(id+"F0.wireOp",EDGE,"E13.4.7"),sQuery(id+"F0.wireOp",EDGE,"E13.4.8"),sQuery(id+"F0.wireOp",EDGE,"E13.4.9"),sQuery(id+"F0.wireOp",EDGE,"E13.4.10"),sQuery(id+"F0.wireOp",EDGE,"E13.4.11"),sQuery(id+"F0.wireOp",EDGE,"E13.5.0"),sQuery(id+"F0.wireOp",EDGE,"E13.5.1"),sQuery(id+"F0.wireOp",EDGE,"E13.5.2"),sQuery(id+"F0.wireOp",EDGE,"E13.5.3"),sQuery(id+"F0.wireOp",EDGE,"E13.5.4"),sQuery(id+"F0.wireOp",EDGE,"E13.5.5"),sQuery(id+"F0.wireOp",EDGE,"E13.5.6"),sQuery(id+"F0.wireOp",EDGE,"E13.5.7"),sQuery(id+"F0.wireOp",EDGE,"E13.5.8"),sQuery(id+"F0.wireOp",EDGE,"E13.5.9"),sQuery(id+"F0.wireOp",EDGE,"E13.5.10"),sQuery(id+"F0.wireOp",EDGE,"E13.5.11"),sQuery(id+"F0.wireOp",EDGE,"E13.6.0"),sQuery(id+"F0.wireOp",EDGE,"E13.6.1"),sQuery(id+"F0.wireOp",EDGE,"E13.6.2"),sQuery(id+"F0.wireOp",EDGE,"E13.6.3"),sQuery(id+"F0.wireOp",EDGE,"E13.6.4"),sQuery(id+"F0.wireOp",EDGE,"E13.6.5"),sQuery(id+"F0.wireOp",EDGE,"E13.6.6"),sQuery(id+"F0.wireOp",EDGE,"E13.6.7"),sQuery(id+"F0.wireOp",EDGE,"E13.6.8"),sQuery(id+"F0.wireOp",EDGE,"E13.6.9"),sQuery(id+"F0.wireOp",EDGE,"E13.6.10"),sQuery(id+"F0.wireOp",EDGE,"E13.6.11"),sQuery(id+"F0.wireOp",EDGE,"E13.7.0"),sQuery(id+"F0.wireOp",EDGE,"E13.7.1"),sQuery(id+"F0.wireOp",EDGE,"E13.7.2"),sQuery(id+"F0.wireOp",EDGE,"E13.7.3"),sQuery(id+"F0.wireOp",EDGE,"E13.7.4"),sQuery(id+"F0.wireOp",EDGE,"E13.7.5"),sQuery(id+"F0.wireOp",EDGE,"E13.7.6"),sQuery(id+"F0.wireOp",EDGE,"E13.7.7"),sQuery(id+"F0.wireOp",EDGE,"E13.7.8"),sQuery(id+"F0.wireOp",EDGE,"E13.7.9"),sQuery(id+"F0.wireOp",EDGE,"E13.7.10"),sQuery(id+"F0.wireOp",EDGE,"E13.7.11"),sQuery(id+"F0.wireOp",EDGE,"E13.8.0"),sQuery(id+"F0.wireOp",EDGE,"E13.8.1"),sQuery(id+"F0.wireOp",EDGE,"E13.8.2"),sQuery(id+"F0.wireOp",EDGE,"E13.8.3"),sQuery(id+"F0.wireOp",EDGE,"E13.8.4"),sQuery(id+"F0.wireOp",EDGE,"E13.8.5"),sQuery(id+"F0.wireOp",EDGE,"E13.8.6"),sQuery(id+"F0.wireOp",EDGE,"E13.8.7"),sQuery(id+"F0.wireOp",EDGE,"E13.8.8"),sQuery(id+"F0.wireOp",EDGE,"E13.8.9"),sQuery(id+"F0.wireOp",EDGE,"E13.8.10"),sQuery(id+"F0.wireOp",EDGE,"E13.8.11"),sQuery(id+"F0.wireOp",EDGE,"E13.9.0"),sQuery(id+"F0.wireOp",EDGE,"E13.9.1"),sQuery(id+"F0.wireOp",EDGE,"E13.9.2"),sQuery(id+"F0.wireOp",EDGE,"E13.9.3"),sQuery(id+"F0.wireOp",EDGE,"E13.9.4"),sQuery(id+"F0.wireOp",EDGE,"E13.9.5"),sQuery(id+"F0.wireOp",EDGE,"E13.9.6"),sQuery(id+"F0.wireOp",EDGE,"E13.9.7"),sQuery(id+"F0.wireOp",EDGE,"E13.9.8"),sQuery(id+"F0.wireOp",EDGE,"E13.9.9"),sQuery(id+"F0.wireOp",EDGE,"E13.9.10"),sQuery(id+"F0.wireOp",EDGE,"E13.9.11"),sQuery(id+"F0.wireOp",EDGE,"E13.10.0"),sQuery(id+"F0.wireOp",EDGE,"E13.10.1"),sQuery(id+"F0.wireOp",EDGE,"E13.10.2"),sQuery(id+"F0.wireOp",EDGE,"E13.10.3"),sQuery(id+"F0.wireOp",EDGE,"E13.10.4"),sQuery(id+"F0.wireOp",EDGE,"E13.10.5"),sQuery(id+"F0.wireOp",EDGE,"E13.10.6"),sQuery(id+"F0.wireOp",EDGE,"E13.10.7"),sQuery(id+"F0.wireOp",EDGE,"E13.10.8"),sQuery(id+"F0.wireOp",EDGE,"E13.10.9"),sQuery(id+"F0.wireOp",EDGE,"E13.10.10"),sQuery(id+"F0.wireOp",EDGE,"E13.10.11"),sQuery(id+"F0.wireOp",EDGE,"E13.11.0"),sQuery(id+"F0.wireOp",EDGE,"E13.11.1"),sQuery(id+"F0.wireOp",EDGE,"E13.11.2"),sQuery(id+"F0.wireOp",EDGE,"E13.11.3"),sQuery(id+"F0.wireOp",EDGE,"E13.11.4"),sQuery(id+"F0.wireOp",EDGE,"E13.11.5"),sQuery(id+"F0.wireOp",EDGE,"E13.11.6"),sQuery(id+"F0.wireOp",EDGE,"E13.11.7"),sQuery(id+"F0.wireOp",EDGE,"E13.11.8"),sQuery(id+"F0.wireOp",EDGE,"E13.11.9"),sQuery(id+"F0.wireOp",EDGE,"E13.11.10"),sQuery(id+"F0.wireOp",EDGE,"E13.11.11"),sQuery(id+"F0.wireOp",EDGE,"E13.12.0"),sQuery(id+"F0.wireOp",EDGE,"E13.12.1"),sQuery(id+"F0.wireOp",EDGE,"E13.12.2"),sQuery(id+"F0.wireOp",EDGE,"E13.12.3"),sQuery(id+"F0.wireOp",EDGE,"E13.12.4"),sQuery(id+"F0.wireOp",EDGE,"E13.12.5"),sQuery(id+"F0.wireOp",EDGE,"E13.12.6"),sQuery(id+"F0.wireOp",EDGE,"E13.12.7"),sQuery(id+"F0.wireOp",EDGE,"E13.12.8"),sQuery(id+"F0.wireOp",EDGE,"E13.12.9"),sQuery(id+"F0.wireOp",EDGE,"E13.12.10"),sQuery(id+"F0.wireOp",EDGE,"E13.12.11"),sQuery(id+"F0.wireOp",EDGE,"E13.13.0"),sQuery(id+"F0.wireOp",EDGE,"E13.13.1"),sQuery(id+"F0.wireOp",EDGE,"E13.13.2"),sQuery(id+"F0.wireOp",EDGE,"E13.13.3"),sQuery(id+"F0.wireOp",EDGE,"E13.13.4"),sQuery(id+"F0.wireOp",EDGE,"E13.13.5"),sQuery(id+"F0.wireOp",EDGE,"E13.13.6"),sQuery(id+"F0.wireOp",EDGE,"E13.13.7"),sQuery(id+"F0.wireOp",EDGE,"E13.13.8"),sQuery(id+"F0.wireOp",EDGE,"E13.13.9"),sQuery(id+"F0.wireOp",EDGE,"E13.13.10"),sQuery(id+"F0.wireOp",EDGE,"E13.13.11"),sQuery(id+"F0.wireOp",EDGE,"E13.14.0"),sQuery(id+"F0.wireOp",EDGE,"E13.14.1"),sQuery(id+"F0.wireOp",EDGE,"E13.14.2"),sQuery(id+"F0.wireOp",EDGE,"E13.14.3"),sQuery(id+"F0.wireOp",EDGE,"E13.14.4"),sQuery(id+"F0.wireOp",EDGE,"E13.14.5"),sQuery(id+"F0.wireOp",EDGE,"E13.14.6"),sQuery(id+"F0.wireOp",EDGE,"E13.14.7"),sQuery(id+"F0.wireOp",EDGE,"E13.14.8"),sQuery(id+"F0.wireOp",EDGE,"E13.14.9"),sQuery(id+"F0.wireOp",EDGE,"E13.14.10"),sQuery(id+"F0.wireOp",EDGE,"E13.14.11"),sQuery(id+"F0.wireOp",EDGE,"E13.15.0"),sQuery(id+"F0.wireOp",EDGE,"E13.15.1"),sQuery(id+"F0.wireOp",EDGE,"E13.15.2"),sQuery(id+"F0.wireOp",EDGE,"E13.15.3"),sQuery(id+"F0.wireOp",EDGE,"E13.15.4"),sQuery(id+"F0.wireOp",EDGE,"E13.15.5"),sQuery(id+"F0.wireOp",EDGE,"E13.15.6"),sQuery(id+"F0.wireOp",EDGE,"E13.15.7"),sQuery(id+"F0.wireOp",EDGE,"E13.15.8"),sQuery(id+"F0.wireOp",EDGE,"E13.15.9"),sQuery(id+"F0.wireOp",EDGE,"E13.15.10"),sQuery(id+"F0.wireOp",EDGE,"E13.15.11"),sQuery(id+"F0.wireOp",EDGE,"E13.16.0"),sQuery(id+"F0.wireOp",EDGE,"E13.16.1"),sQuery(id+"F0.wireOp",EDGE,"E13.16.2"),sQuery(id+"F0.wireOp",EDGE,"E13.16.3"),sQuery(id+"F0.wireOp",EDGE,"E13.16.4"),sQuery(id+"F0.wireOp",EDGE,"E13.16.5"),sQuery(id+"F0.wireOp",EDGE,"E13.16.6"),sQuery(id+"F0.wireOp",EDGE,"E13.16.7"),sQuery(id+"F0.wireOp",EDGE,"E13.16.8"),sQuery(id+"F0.wireOp",EDGE,"E13.16.9"),sQuery(id+"F0.wireOp",EDGE,"E13.16.10"),sQuery(id+"F0.wireOp",EDGE,"E13.16.11"),sQuery(id+"F0.wireOp",EDGE,"E13.17.0"),sQuery(id+"F0.wireOp",EDGE,"E13.17.1"),sQuery(id+"F0.wireOp",EDGE,"E13.17.2"),sQuery(id+"F0.wireOp",EDGE,"E13.17.3"),sQuery(id+"F0.wireOp",EDGE,"E13.17.4"),sQuery(id+"F0.wireOp",EDGE,"E13.17.5"),sQuery(id+"F0.wireOp",EDGE,"E13.17.6"),sQuery(id+"F0.wireOp",EDGE,"E13.17.7"),sQuery(id+"F0.wireOp",EDGE,"E13.17.8"),sQuery(id+"F0.wireOp",EDGE,"E13.17.9"),sQuery(id+"F0.wireOp",EDGE,"E13.17.10"),sQuery(id+"F0.wireOp",EDGE,"E13.17.11"),sQuery(id+"F0.wireOp",EDGE,"E13.18.0"),sQuery(id+"F0.wireOp",EDGE,"E13.18.1"),sQuery(id+"F0.wireOp",EDGE,"E13.18.2"),sQuery(id+"F0.wireOp",EDGE,"E13.18.3"),sQuery(id+"F0.wireOp",EDGE,"E13.18.4"),sQuery(id+"F0.wireOp",EDGE,"E13.18.5"),sQuery(id+"F0.wireOp",EDGE,"E13.18.6"),sQuery(id+"F0.wireOp",EDGE,"E13.18.7"),sQuery(id+"F0.wireOp",EDGE,"E13.18.8"),sQuery(id+"F0.wireOp",EDGE,"E13.18.9"),sQuery(id+"F0.wireOp",EDGE,"E13.18.10"),sQuery(id+"F0.wireOp",EDGE,"E13.18.11"),sQuery(id+"F0.wireOp",EDGE,"E13.19.0"),sQuery(id+"F0.wireOp",EDGE,"E13.19.1"),sQuery(id+"F0.wireOp",EDGE,"E13.19.2"),sQuery(id+"F0.wireOp",EDGE,"E13.19.3"),sQuery(id+"F0.wireOp",EDGE,"E13.19.4"),sQuery(id+"F0.wireOp",EDGE,"E13.19.5"),sQuery(id+"F0.wireOp",EDGE,"E13.19.6"),sQuery(id+"F0.wireOp",EDGE,"E13.19.7"),sQuery(id+"F0.wireOp",EDGE,"E13.19.8"),sQuery(id+"F0.wireOp",EDGE,"E13.19.9"),sQuery(id+"F0.wireOp",EDGE,"E13.19.10"),sQuery(id+"F0.wireOp",EDGE,"E13.19.11"),sQuery(id+"F0.wireOp",EDGE,"E13.20.0"),sQuery(id+"F0.wireOp",EDGE,"E13.20.1"),sQuery(id+"F0.wireOp",EDGE,"E13.20.2"),sQuery(id+"F0.wireOp",EDGE,"E13.20.3"),sQuery(id+"F0.wireOp",EDGE,"E13.20.4"),sQuery(id+"F0.wireOp",EDGE,"E13.20.5"),sQuery(id+"F0.wireOp",EDGE,"E13.20.6"),sQuery(id+"F0.wireOp",EDGE,"E13.20.7"),sQuery(id+"F0.wireOp",EDGE,"E13.20.8"),sQuery(id+"F0.wireOp",EDGE,"E13.20.9"),sQuery(id+"F0.wireOp",EDGE,"E13.20.10"),sQuery(id+"F0.wireOp",EDGE,"E13.20.11"),sQuery(id+"F0.wireOp",EDGE,"E13.21.0"),sQuery(id+"F0.wireOp",EDGE,"E13.21.1"),sQuery(id+"F0.wireOp",EDGE,"E13.21.2"),sQuery(id+"F0.wireOp",EDGE,"E13.21.3"),sQuery(id+"F0.wireOp",EDGE,"E13.21.4"),sQuery(id+"F0.wireOp",EDGE,"E13.21.5"),sQuery(id+"F0.wireOp",EDGE,"E13.21.6"),sQuery(id+"F0.wireOp",EDGE,"E13.21.7"),sQuery(id+"F0.wireOp",EDGE,"E13.21.8"),sQuery(id+"F0.wireOp",EDGE,"E13.21.9"),sQuery(id+"F0.wireOp",EDGE,"E13.21.10"),sQuery(id+"F0.wireOp",EDGE,"E13.21.11"),sQuery(id+"F0.wireOp",EDGE,"E13.22.0"),sQuery(id+"F0.wireOp",EDGE,"E13.22.1"),sQuery(id+"F0.wireOp",EDGE,"E13.22.2"),sQuery(id+"F0.wireOp",EDGE,"E13.22.3"),sQuery(id+"F0.wireOp",EDGE,"E13.22.4"),sQuery(id+"F0.wireOp",EDGE,"E13.22.5"),sQuery(id+"F0.wireOp",EDGE,"E13.22.6"),sQuery(id+"F0.wireOp",EDGE,"E13.22.7"),sQuery(id+"F0.wireOp",EDGE,"E13.22.8"),sQuery(id+"F0.wireOp",EDGE,"E13.22.9"),sQuery(id+"F0.wireOp",EDGE,"E13.22.10"),sQuery(id+"F0.wireOp",EDGE,"E13.22.11"),sQuery(id+"F0.wireOp",EDGE,"E13.23.0"),sQuery(id+"F0.wireOp",EDGE,"E13.23.1"),sQuery(id+"F0.wireOp",EDGE,"E13.23.2"),sQuery(id+"F0.wireOp",EDGE,"E13.23.3"),sQuery(id+"F0.wireOp",EDGE,"E13.23.4"),sQuery(id+"F0.wireOp",EDGE,"E13.23.5"),sQuery(id+"F0.wireOp",EDGE,"E13.23.6"),sQuery(id+"F0.wireOp",EDGE,"E13.23.7"),sQuery(id+"F0.wireOp",EDGE,"E13.23.8"),sQuery(id+"F0.wireOp",EDGE,"E13.23.9"),sQuery(id+"F0.wireOp",EDGE,"E13.23.10"),sQuery(id+"F0.wireOp",EDGE,"E13.23.11"),sQuery(id+"F0.wireOp",EDGE,"E13.24.0"),sQuery(id+"F0.wireOp",EDGE,"E13.24.1"),sQuery(id+"F0.wireOp",EDGE,"E13.24.2"),sQuery(id+"F0.wireOp",EDGE,"E13.24.3"),sQuery(id+"F0.wireOp",EDGE,"E13.24.4"),sQuery(id+"F0.wireOp",EDGE,"E13.24.5"),sQuery(id+"F0.wireOp",EDGE,"E13.24.6"),sQuery(id+"F0.wireOp",EDGE,"E13.24.7"),sQuery(id+"F0.wireOp",EDGE,"E13.24.8"),sQuery(id+"F0.wireOp",EDGE,"E13.24.9"),sQuery(id+"F0.wireOp",EDGE,"E13.24.10"),sQuery(id+"F0.wireOp",EDGE,"E13.24.11"),sQuery(id+"F0.wireOp",EDGE,"E13.25.0"),sQuery(id+"F0.wireOp",EDGE,"E13.25.1"),sQuery(id+"F0.wireOp",EDGE,"E13.25.2"),sQuery(id+"F0.wireOp",EDGE,"E13.25.3"),sQuery(id+"F0.wireOp",EDGE,"E13.25.4"),sQuery(id+"F0.wireOp",EDGE,"E13.25.5"),sQuery(id+"F0.wireOp",EDGE,"E13.25.6"),sQuery(id+"F0.wireOp",EDGE,"E13.25.7"),sQuery(id+"F0.wireOp",EDGE,"E13.25.8"),sQuery(id+"F0.wireOp",EDGE,"E13.25.9"),sQuery(id+"F0.wireOp",EDGE,"E13.25.10"),sQuery(id+"F0.wireOp",EDGE,"E13.25.11"),sQuery(id+"F0.wireOp",EDGE,"E13.26.0"),sQuery(id+"F0.wireOp",EDGE,"E13.26.1"),sQuery(id+"F0.wireOp",EDGE,"E13.26.2"),sQuery(id+"F0.wireOp",EDGE,"E13.26.3"),sQuery(id+"F0.wireOp",EDGE,"E13.26.4"),sQuery(id+"F0.wireOp",EDGE,"E13.26.5"),sQuery(id+"F0.wireOp",EDGE,"E13.26.6"),sQuery(id+"F0.wireOp",EDGE,"E13.26.7"),sQuery(id+"F0.wireOp",EDGE,"E13.26.8"),sQuery(id+"F0.wireOp",EDGE,"E13.26.9"),sQuery(id+"F0.wireOp",EDGE,"E13.26.10"),sQuery(id+"F0.wireOp",EDGE,"E13.26.11"),sQuery(id+"F0.wireOp",EDGE,"E13.27.0"),sQuery(id+"F0.wireOp",EDGE,"E13.27.1"),sQuery(id+"F0.wireOp",EDGE,"E13.27.2"),sQuery(id+"F0.wireOp",EDGE,"E13.27.3"),sQuery(id+"F0.wireOp",EDGE,"E13.27.4"),sQuery(id+"F0.wireOp",EDGE,"E13.27.5"),sQuery(id+"F0.wireOp",EDGE,"E13.27.6"),sQuery(id+"F0.wireOp",EDGE,"E13.27.7"),sQuery(id+"F0.wireOp",EDGE,"E13.27.8"),sQuery(id+"F0.wireOp",EDGE,"E13.27.9"),sQuery(id+"F0.wireOp",EDGE,"E13.27.10"),sQuery(id+"F0.wireOp",EDGE,"E13.27.11"),sQuery(id+"F0.wireOp",EDGE,"E13.28.0"),sQuery(id+"F0.wireOp",EDGE,"E13.28.1"),sQuery(id+"F0.wireOp",EDGE,"E13.28.2"),sQuery(id+"F0.wireOp",EDGE,"E13.28.3"),sQuery(id+"F0.wireOp",EDGE,"E13.28.4"),sQuery(id+"F0.wireOp",EDGE,"E13.28.5"),sQuery(id+"F0.wireOp",EDGE,"E13.28.6"),sQuery(id+"F0.wireOp",EDGE,"E13.28.7"),sQuery(id+"F0.wireOp",EDGE,"E13.28.8"),sQuery(id+"F0.wireOp",EDGE,"E13.28.9"),sQuery(id+"F0.wireOp",EDGE,"E13.28.10"),sQuery(id+"F0.wireOp",EDGE,"E13.28.11"),sQuery(id+"F0.wireOp",EDGE,"E13.29.0"),sQuery(id+"F0.wireOp",EDGE,"E13.29.1"),sQuery(id+"F0.wireOp",EDGE,"E13.29.2"),sQuery(id+"F0.wireOp",EDGE,"E13.29.3"),sQuery(id+"F0.wireOp",EDGE,"E13.29.4"),sQuery(id+"F0.wireOp",EDGE,"E13.29.5"),sQuery(id+"F0.wireOp",EDGE,"E13.29.6"),sQuery(id+"F0.wireOp",EDGE,"E13.29.7"),sQuery(id+"F0.wireOp",EDGE,"E13.29.8"),sQuery(id+"F0.wireOp",EDGE,"E13.29.9"),sQuery(id+"F0.wireOp",EDGE,"E13.29.10"),sQuery(id+"F0.wireOp",EDGE,"E13.29.11"),sQuery(id+"F0.wireOp",EDGE,"E13.30.0"),sQuery(id+"F0.wireOp",EDGE,"E13.30.1"),sQuery(id+"F0.wireOp",EDGE,"E13.30.2"),sQuery(id+"F0.wireOp",EDGE,"E13.30.3"),sQuery(id+"F0.wireOp",EDGE,"E13.30.4"),sQuery(id+"F0.wireOp",EDGE,"E13.30.5"),sQuery(id+"F0.wireOp",EDGE,"E13.30.6"),sQuery(id+"F0.wireOp",EDGE,"E13.30.7"),sQuery(id+"F0.wireOp",EDGE,"E13.30.8"),sQuery(id+"F0.wireOp",EDGE,"E13.30.9"),sQuery(id+"F0.wireOp",EDGE,"E13.30.10"),sQuery(id+"F0.wireOp",EDGE,"E13.30.11"),sQuery(id+"F0.wireOp",EDGE,"E13.31.0"),sQuery(id+"F0.wireOp",EDGE,"E13.31.1"),sQuery(id+"F0.wireOp",EDGE,"E13.31.2"),sQuery(id+"F0.wireOp",EDGE,"E13.31.3"),sQuery(id+"F0.wireOp",EDGE,"E13.31.4"),sQuery(id+"F0.wireOp",EDGE,"E13.31.5"),sQuery(id+"F0.wireOp",EDGE,"E13.31.6"),sQuery(id+"F0.wireOp",EDGE,"E13.31.7"),sQuery(id+"F0.wireOp",EDGE,"E13.31.8"),sQuery(id+"F0.wireOp",EDGE,"E13.31.9"),sQuery(id+"F0.wireOp",EDGE,"E13.31.10"),sQuery(id+"F0.wireOp",EDGE,"E13.31.11"),sQuery(id+"F0.wireOp",EDGE,"E13.32.0"),sQuery(id+"F0.wireOp",EDGE,"E13.32.1"),sQuery(id+"F0.wireOp",EDGE,"E13.32.2"),sQuery(id+"F0.wireOp",EDGE,"E13.32.3"),sQuery(id+"F0.wireOp",EDGE,"E13.32.4"),sQuery(id+"F0.wireOp",EDGE,"E13.32.5"),sQuery(id+"F0.wireOp",EDGE,"E13.32.6"),sQuery(id+"F0.wireOp",EDGE,"E13.32.7"),sQuery(id+"F0.wireOp",EDGE,"E13.32.8"),sQuery(id+"F0.wireOp",EDGE,"E13.32.9"),sQuery(id+"F0.wireOp",EDGE,"E13.32.10"),sQuery(id+"F0.wireOp",EDGE,"E13.32.11"),sQuery(id+"F0.wireOp",EDGE,"E13.33.0"),sQuery(id+"F0.wireOp",EDGE,"E13.33.1"),sQuery(id+"F0.wireOp",EDGE,"E13.33.2"),sQuery(id+"F0.wireOp",EDGE,"E13.33.3"),sQuery(id+"F0.wireOp",EDGE,"E13.33.4"),sQuery(id+"F0.wireOp",EDGE,"E13.33.5"),sQuery(id+"F0.wireOp",EDGE,"E13.33.6"),sQuery(id+"F0.wireOp",EDGE,"E13.33.7"),sQuery(id+"F0.wireOp",EDGE,"E13.33.8"),sQuery(id+"F0.wireOp",EDGE,"E13.33.9"),sQuery(id+"F0.wireOp",EDGE,"E13.33.10"),sQuery(id+"F0.wireOp",EDGE,"E13.33.11"),sQuery(id+"F0.wireOp",EDGE,"E13.34.0"),sQuery(id+"F0.wireOp",EDGE,"E13.34.1"),sQuery(id+"F0.wireOp",EDGE,"E13.34.2"),sQuery(id+"F0.wireOp",EDGE,"E13.34.3"),sQuery(id+"F0.wireOp",EDGE,"E13.34.4"),sQuery(id+"F0.wireOp",EDGE,"E13.34.5"),sQuery(id+"F0.wireOp",EDGE,"E13.34.6"),sQuery(id+"F0.wireOp",EDGE,"E13.34.7"),sQuery(id+"F0.wireOp",EDGE,"E13.34.8"),sQuery(id+"F0.wireOp",EDGE,"E13.34.9"),sQuery(id+"F0.wireOp",EDGE,"E13.34.10"),sQuery(id+"F0.wireOp",EDGE,"E13.34.11"),sQuery(id+"F0.wireOp",EDGE,"E13.35.0"),sQuery(id+"F0.wireOp",EDGE,"E13.35.1"),sQuery(id+"F0.wireOp",EDGE,"E13.35.2"),sQuery(id+"F0.wireOp",EDGE,"E13.35.3"),sQuery(id+"F0.wireOp",EDGE,"E13.35.4"),sQuery(id+"F0.wireOp",EDGE,"E13.35.5"),sQuery(id+"F0.wireOp",EDGE,"E13.35.6"),sQuery(id+"F0.wireOp",EDGE,"E13.35.7"),sQuery(id+"F0.wireOp",EDGE,"E13.35.8"),sQuery(id+"F0.wireOp",EDGE,"E13.35.9"),sQuery(id+"F0.wireOp",EDGE,"E13.35.10"),sQuery(id+"F0.wireOp",EDGE,"E13.35.11"),sQuery(id+"F0.wireOp",EDGE,"E14.trimOffspring"),sQuery(id+"F0.wireOp",EDGE,"E15.trimOffspring"),sQuery(id+"F0.wireOp",EDGE,"E16.trimOffspring"),sQuery(id+"F0.wireOp",EDGE,"E17.trimOffspring"),sQuery(id+"F0.wireOp",EDGE,"E18.trimOffspring"),sQuery(id+"F0.wireOp",EDGE,"E19.trimOffspring"),sQuery(id+"F0.wireOp",EDGE,"E20.trimOffspring"),sQuery(id+"F0.wireOp",EDGE,"E21.trimOffspring"),sQuery(id+"F0.wireOp",EDGE,"E22.trimOffspring"),sQuery(id+"F0.wireOp",EDGE,"E23.trimOffspring"),sQuery(id+"F0.wireOp",EDGE,"E24.trimOffspring"),sQuery(id+"F0.wireOp",EDGE,"E25.trimOffspring"),sQuery(id+"F0.wireOp",EDGE,"E26.trimOffspring"),sQuery(id+"F0.wireOp",EDGE,"E27.trimOffspring"),sQuery(id+"F0.wireOp",EDGE,"E28.trimOffspring"),sQuery(id+"F0.wireOp",EDGE,"E29.trimOffspring"),sQuery(id+"F0.wireOp",EDGE,"E30.trimOffspring"),sQuery(id+"F0.wireOp",EDGE,"E31.trimOffspring"),sQuery(id+"F0.wireOp",EDGE,"E32.trimOffspring"),sQuery(id+"F0.wireOp",EDGE,"E33.trimOffspring"),sQuery(id+"F0.wireOp",EDGE,"E34.trimOffspring"),sQuery(id+"F0.wireOp",EDGE,"E35.trimOffspring"),sQuery(id+"F0.wireOp",EDGE,"E36.trimOffspring"),sQuery(id+"F0.wireOp",EDGE,"E37.trimOffspring"),sQuery(id+"F0.wireOp",EDGE,"E38.trimOffspring"),sQuery(id+"F0.wireOp",EDGE,"E39.trimOffspring"),sQuery(id+"F0.wireOp",EDGE,"E40.trimOffspring"),sQuery(id+"F0.wireOp",EDGE,"E41.trimOffspring"),sQuery(id+"F0.wireOp",EDGE,"E42.trimOffspring"),sQuery(id+"F0.wireOp",EDGE,"E43.trimOffspring"),sQuery(id+"F0.wireOp",EDGE,"E44.trimOffspring"),sQuery(id+"F0.wireOp",EDGE,"E45.trimOffspring"),sQuery(id+"F0.wireOp",EDGE,"E46.trimOffspring"),sQuery(id+"F0.wireOp",EDGE,"E47"),sQuery(id+"F0.wireOp",EDGE,"E48"),sQuery(id+"F0.wireOp",EDGE,"E49")])],"isStart":false});
            var sketch = newSketch(context, id + "F2", { "sketchPlane" : qUnion([Q0])});
            skCircle(sketch, "E50", {"center": v(0, 0) * mm, "radius": 3.18 * mm});
            skSolve(sketch);
        }
        {
            var Q0;
            Q0 = qSketchRegion(id + "F2", true);
            extrude(context, id + "F3", {"entities" : qUnion([Q0]), "operationType" : NewBodyOperationType.REMOVE, "endBound" : BoundingType.THROUGH_ALL, "oppositeDirection" : true, "depth" : 25.4 * mm});
        }
        {
            var Q0;
            Q0=makeQuery(id+"F1.opExtrude","CAP_FACE",FACE,{"disambiguationData":[OSD([sQuery(id+"F0.wireOp",EDGE,"E1.trimOffspring"),sQuery(id+"F0.wireOp",EDGE,"E2"),sQuery(id+"F0.wireOp",EDGE,"E3"),sQuery(id+"F0.wireOp",EDGE,"E4.MirrorCS"),sQuery(id+"F0.wireOp",EDGE,"E5.MirrorCS"),sQuery(id+"F0.wireOp",EDGE,"E6.MirrorCS"),sQuery(id+"F0.wireOp",EDGE,"E7.filletArc"),sQuery(id+"F0.wireOp",EDGE,"E8.filletArc"),sQuery(id+"F0.wireOp",EDGE,"E9.filletArc"),sQuery(id+"F0.wireOp",EDGE,"E10.filletArc"),sQuery(id+"F0.wireOp",EDGE,"E11.filletArc"),sQuery(id+"F0.wireOp",EDGE,"E12.filletArc"),sQuery(id+"F0.wireOp",EDGE,"E13.1.0"),sQuery(id+"F0.wireOp",EDGE,"E13.1.1"),sQuery(id+"F0.wireOp",EDGE,"E13.1.2"),sQuery(id+"F0.wireOp",EDGE,"E13.1.3"),sQuery(id+"F0.wireOp",EDGE,"E13.1.4"),sQuery(id+"F0.wireOp",EDGE,"E13.1.5"),sQuery(id+"F0.wireOp",EDGE,"E13.1.6"),sQuery(id+"F0.wireOp",EDGE,"E13.1.7"),sQuery(id+"F0.wireOp",EDGE,"E13.1.8"),sQuery(id+"F0.wireOp",EDGE,"E13.1.9"),sQuery(id+"F0.wireOp",EDGE,"E13.1.10"),sQuery(id+"F0.wireOp",EDGE,"E13.1.11"),sQuery(id+"F0.wireOp",EDGE,"E13.2.0"),sQuery(id+"F0.wireOp",EDGE,"E13.2.1"),sQuery(id+"F0.wireOp",EDGE,"E13.2.2"),sQuery(id+"F0.wireOp",EDGE,"E13.2.3"),sQuery(id+"F0.wireOp",EDGE,"E13.2.4"),sQuery(id+"F0.wireOp",EDGE,"E13.2.5"),sQuery(id+"F0.wireOp",EDGE,"E13.2.6"),sQuery(id+"F0.wireOp",EDGE,"E13.2.7"),sQuery(id+"F0.wireOp",EDGE,"E13.2.8"),sQuery(id+"F0.wireOp",EDGE,"E13.2.9"),sQuery(id+"F0.wireOp",EDGE,"E13.2.10"),sQuery(id+"F0.wireOp",EDGE,"E13.2.11"),sQuery(id+"F0.wireOp",EDGE,"E13.3.0"),sQuery(id+"F0.wireOp",EDGE,"E13.3.1"),sQuery(id+"F0.wireOp",EDGE,"E13.3.2"),sQuery(id+"F0.wireOp",EDGE,"E13.3.3"),sQuery(id+"F0.wireOp",EDGE,"E13.3.4"),sQuery(id+"F0.wireOp",EDGE,"E13.3.5"),sQuery(id+"F0.wireOp",EDGE,"E13.3.6"),sQuery(id+"F0.wireOp",EDGE,"E13.3.7"),sQuery(id+"F0.wireOp",EDGE,"E13.3.8"),sQuery(id+"F0.wireOp",EDGE,"E13.3.9"),sQuery(id+"F0.wireOp",EDGE,"E13.3.10"),sQuery(id+"F0.wireOp",EDGE,"E13.3.11"),sQuery(id+"F0.wireOp",EDGE,"E13.4.0"),sQuery(id+"F0.wireOp",EDGE,"E13.4.1"),sQuery(id+"F0.wireOp",EDGE,"E13.4.2"),sQuery(id+"F0.wireOp",EDGE,"E13.4.3"),sQuery(id+"F0.wireOp",EDGE,"E13.4.4"),sQuery(id+"F0.wireOp",EDGE,"E13.4.5"),sQuery(id+"F0.wireOp",EDGE,"E13.4.6"),sQuery(id+"F0.wireOp",EDGE,"E13.4.7"),sQuery(id+"F0.wireOp",EDGE,"E13.4.8"),sQuery(id+"F0.wireOp",EDGE,"E13.4.9"),sQuery(id+"F0.wireOp",EDGE,"E13.4.10"),sQuery(id+"F0.wireOp",EDGE,"E13.4.11"),sQuery(id+"F0.wireOp",EDGE,"E13.5.0"),sQuery(id+"F0.wireOp",EDGE,"E13.5.1"),sQuery(id+"F0.wireOp",EDGE,"E13.5.2"),sQuery(id+"F0.wireOp",EDGE,"E13.5.3"),sQuery(id+"F0.wireOp",EDGE,"E13.5.4"),sQuery(id+"F0.wireOp",EDGE,"E13.5.5"),sQuery(id+"F0.wireOp",EDGE,"E13.5.6"),sQuery(id+"F0.wireOp",EDGE,"E13.5.7"),sQuery(id+"F0.wireOp",EDGE,"E13.5.8"),sQuery(id+"F0.wireOp",EDGE,"E13.5.9"),sQuery(id+"F0.wireOp",EDGE,"E13.5.10"),sQuery(id+"F0.wireOp",EDGE,"E13.5.11"),sQuery(id+"F0.wireOp",EDGE,"E13.6.0"),sQuery(id+"F0.wireOp",EDGE,"E13.6.1"),sQuery(id+"F0.wireOp",EDGE,"E13.6.2"),sQuery(id+"F0.wireOp",EDGE,"E13.6.3"),sQuery(id+"F0.wireOp",EDGE,"E13.6.4"),sQuery(id+"F0.wireOp",EDGE,"E13.6.5"),sQuery(id+"F0.wireOp",EDGE,"E13.6.6"),sQuery(id+"F0.wireOp",EDGE,"E13.6.7"),sQuery(id+"F0.wireOp",EDGE,"E13.6.8"),sQuery(id+"F0.wireOp",EDGE,"E13.6.9"),sQuery(id+"F0.wireOp",EDGE,"E13.6.10"),sQuery(id+"F0.wireOp",EDGE,"E13.6.11"),sQuery(id+"F0.wireOp",EDGE,"E13.7.0"),sQuery(id+"F0.wireOp",EDGE,"E13.7.1"),sQuery(id+"F0.wireOp",EDGE,"E13.7.2"),sQuery(id+"F0.wireOp",EDGE,"E13.7.3"),sQuery(id+"F0.wireOp",EDGE,"E13.7.4"),sQuery(id+"F0.wireOp",EDGE,"E13.7.5"),sQuery(id+"F0.wireOp",EDGE,"E13.7.6"),sQuery(id+"F0.wireOp",EDGE,"E13.7.7"),sQuery(id+"F0.wireOp",EDGE,"E13.7.8"),sQuery(id+"F0.wireOp",EDGE,"E13.7.9"),sQuery(id+"F0.wireOp",EDGE,"E13.7.10"),sQuery(id+"F0.wireOp",EDGE,"E13.7.11"),sQuery(id+"F0.wireOp",EDGE,"E13.8.0"),sQuery(id+"F0.wireOp",EDGE,"E13.8.1"),sQuery(id+"F0.wireOp",EDGE,"E13.8.2"),sQuery(id+"F0.wireOp",EDGE,"E13.8.3"),sQuery(id+"F0.wireOp",EDGE,"E13.8.4"),sQuery(id+"F0.wireOp",EDGE,"E13.8.5"),sQuery(id+"F0.wireOp",EDGE,"E13.8.6"),sQuery(id+"F0.wireOp",EDGE,"E13.8.7"),sQuery(id+"F0.wireOp",EDGE,"E13.8.8"),sQuery(id+"F0.wireOp",EDGE,"E13.8.9"),sQuery(id+"F0.wireOp",EDGE,"E13.8.10"),sQuery(id+"F0.wireOp",EDGE,"E13.8.11"),sQuery(id+"F0.wireOp",EDGE,"E13.9.0"),sQuery(id+"F0.wireOp",EDGE,"E13.9.1"),sQuery(id+"F0.wireOp",EDGE,"E13.9.2"),sQuery(id+"F0.wireOp",EDGE,"E13.9.3"),sQuery(id+"F0.wireOp",EDGE,"E13.9.4"),sQuery(id+"F0.wireOp",EDGE,"E13.9.5"),sQuery(id+"F0.wireOp",EDGE,"E13.9.6"),sQuery(id+"F0.wireOp",EDGE,"E13.9.7"),sQuery(id+"F0.wireOp",EDGE,"E13.9.8"),sQuery(id+"F0.wireOp",EDGE,"E13.9.9"),sQuery(id+"F0.wireOp",EDGE,"E13.9.10"),sQuery(id+"F0.wireOp",EDGE,"E13.9.11"),sQuery(id+"F0.wireOp",EDGE,"E13.10.0"),sQuery(id+"F0.wireOp",EDGE,"E13.10.1"),sQuery(id+"F0.wireOp",EDGE,"E13.10.2"),sQuery(id+"F0.wireOp",EDGE,"E13.10.3"),sQuery(id+"F0.wireOp",EDGE,"E13.10.4"),sQuery(id+"F0.wireOp",EDGE,"E13.10.5"),sQuery(id+"F0.wireOp",EDGE,"E13.10.6"),sQuery(id+"F0.wireOp",EDGE,"E13.10.7"),sQuery(id+"F0.wireOp",EDGE,"E13.10.8"),sQuery(id+"F0.wireOp",EDGE,"E13.10.9"),sQuery(id+"F0.wireOp",EDGE,"E13.10.10"),sQuery(id+"F0.wireOp",EDGE,"E13.10.11"),sQuery(id+"F0.wireOp",EDGE,"E13.11.0"),sQuery(id+"F0.wireOp",EDGE,"E13.11.1"),sQuery(id+"F0.wireOp",EDGE,"E13.11.2"),sQuery(id+"F0.wireOp",EDGE,"E13.11.3"),sQuery(id+"F0.wireOp",EDGE,"E13.11.4"),sQuery(id+"F0.wireOp",EDGE,"E13.11.5"),sQuery(id+"F0.wireOp",EDGE,"E13.11.6"),sQuery(id+"F0.wireOp",EDGE,"E13.11.7"),sQuery(id+"F0.wireOp",EDGE,"E13.11.8"),sQuery(id+"F0.wireOp",EDGE,"E13.11.9"),sQuery(id+"F0.wireOp",EDGE,"E13.11.10"),sQuery(id+"F0.wireOp",EDGE,"E13.11.11"),sQuery(id+"F0.wireOp",EDGE,"E13.12.0"),sQuery(id+"F0.wireOp",EDGE,"E13.12.1"),sQuery(id+"F0.wireOp",EDGE,"E13.12.2"),sQuery(id+"F0.wireOp",EDGE,"E13.12.3"),sQuery(id+"F0.wireOp",EDGE,"E13.12.4"),sQuery(id+"F0.wireOp",EDGE,"E13.12.5"),sQuery(id+"F0.wireOp",EDGE,"E13.12.6"),sQuery(id+"F0.wireOp",EDGE,"E13.12.7"),sQuery(id+"F0.wireOp",EDGE,"E13.12.8"),sQuery(id+"F0.wireOp",EDGE,"E13.12.9"),sQuery(id+"F0.wireOp",EDGE,"E13.12.10"),sQuery(id+"F0.wireOp",EDGE,"E13.12.11"),sQuery(id+"F0.wireOp",EDGE,"E13.13.0"),sQuery(id+"F0.wireOp",EDGE,"E13.13.1"),sQuery(id+"F0.wireOp",EDGE,"E13.13.2"),sQuery(id+"F0.wireOp",EDGE,"E13.13.3"),sQuery(id+"F0.wireOp",EDGE,"E13.13.4"),sQuery(id+"F0.wireOp",EDGE,"E13.13.5"),sQuery(id+"F0.wireOp",EDGE,"E13.13.6"),sQuery(id+"F0.wireOp",EDGE,"E13.13.7"),sQuery(id+"F0.wireOp",EDGE,"E13.13.8"),sQuery(id+"F0.wireOp",EDGE,"E13.13.9"),sQuery(id+"F0.wireOp",EDGE,"E13.13.10"),sQuery(id+"F0.wireOp",EDGE,"E13.13.11"),sQuery(id+"F0.wireOp",EDGE,"E13.14.0"),sQuery(id+"F0.wireOp",EDGE,"E13.14.1"),sQuery(id+"F0.wireOp",EDGE,"E13.14.2"),sQuery(id+"F0.wireOp",EDGE,"E13.14.3"),sQuery(id+"F0.wireOp",EDGE,"E13.14.4"),sQuery(id+"F0.wireOp",EDGE,"E13.14.5"),sQuery(id+"F0.wireOp",EDGE,"E13.14.6"),sQuery(id+"F0.wireOp",EDGE,"E13.14.7"),sQuery(id+"F0.wireOp",EDGE,"E13.14.8"),sQuery(id+"F0.wireOp",EDGE,"E13.14.9"),sQuery(id+"F0.wireOp",EDGE,"E13.14.10"),sQuery(id+"F0.wireOp",EDGE,"E13.14.11"),sQuery(id+"F0.wireOp",EDGE,"E13.15.0"),sQuery(id+"F0.wireOp",EDGE,"E13.15.1"),sQuery(id+"F0.wireOp",EDGE,"E13.15.2"),sQuery(id+"F0.wireOp",EDGE,"E13.15.3"),sQuery(id+"F0.wireOp",EDGE,"E13.15.4"),sQuery(id+"F0.wireOp",EDGE,"E13.15.5"),sQuery(id+"F0.wireOp",EDGE,"E13.15.6"),sQuery(id+"F0.wireOp",EDGE,"E13.15.7"),sQuery(id+"F0.wireOp",EDGE,"E13.15.8"),sQuery(id+"F0.wireOp",EDGE,"E13.15.9"),sQuery(id+"F0.wireOp",EDGE,"E13.15.10"),sQuery(id+"F0.wireOp",EDGE,"E13.15.11"),sQuery(id+"F0.wireOp",EDGE,"E13.16.0"),sQuery(id+"F0.wireOp",EDGE,"E13.16.1"),sQuery(id+"F0.wireOp",EDGE,"E13.16.2"),sQuery(id+"F0.wireOp",EDGE,"E13.16.3"),sQuery(id+"F0.wireOp",EDGE,"E13.16.4"),sQuery(id+"F0.wireOp",EDGE,"E13.16.5"),sQuery(id+"F0.wireOp",EDGE,"E13.16.6"),sQuery(id+"F0.wireOp",EDGE,"E13.16.7"),sQuery(id+"F0.wireOp",EDGE,"E13.16.8"),sQuery(id+"F0.wireOp",EDGE,"E13.16.9"),sQuery(id+"F0.wireOp",EDGE,"E13.16.10"),sQuery(id+"F0.wireOp",EDGE,"E13.16.11"),sQuery(id+"F0.wireOp",EDGE,"E13.17.0"),sQuery(id+"F0.wireOp",EDGE,"E13.17.1"),sQuery(id+"F0.wireOp",EDGE,"E13.17.2"),sQuery(id+"F0.wireOp",EDGE,"E13.17.3"),sQuery(id+"F0.wireOp",EDGE,"E13.17.4"),sQuery(id+"F0.wireOp",EDGE,"E13.17.5"),sQuery(id+"F0.wireOp",EDGE,"E13.17.6"),sQuery(id+"F0.wireOp",EDGE,"E13.17.7"),sQuery(id+"F0.wireOp",EDGE,"E13.17.8"),sQuery(id+"F0.wireOp",EDGE,"E13.17.9"),sQuery(id+"F0.wireOp",EDGE,"E13.17.10"),sQuery(id+"F0.wireOp",EDGE,"E13.17.11"),sQuery(id+"F0.wireOp",EDGE,"E13.18.0"),sQuery(id+"F0.wireOp",EDGE,"E13.18.1"),sQuery(id+"F0.wireOp",EDGE,"E13.18.2"),sQuery(id+"F0.wireOp",EDGE,"E13.18.3"),sQuery(id+"F0.wireOp",EDGE,"E13.18.4"),sQuery(id+"F0.wireOp",EDGE,"E13.18.5"),sQuery(id+"F0.wireOp",EDGE,"E13.18.6"),sQuery(id+"F0.wireOp",EDGE,"E13.18.7"),sQuery(id+"F0.wireOp",EDGE,"E13.18.8"),sQuery(id+"F0.wireOp",EDGE,"E13.18.9"),sQuery(id+"F0.wireOp",EDGE,"E13.18.10"),sQuery(id+"F0.wireOp",EDGE,"E13.18.11"),sQuery(id+"F0.wireOp",EDGE,"E13.19.0"),sQuery(id+"F0.wireOp",EDGE,"E13.19.1"),sQuery(id+"F0.wireOp",EDGE,"E13.19.2"),sQuery(id+"F0.wireOp",EDGE,"E13.19.3"),sQuery(id+"F0.wireOp",EDGE,"E13.19.4"),sQuery(id+"F0.wireOp",EDGE,"E13.19.5"),sQuery(id+"F0.wireOp",EDGE,"E13.19.6"),sQuery(id+"F0.wireOp",EDGE,"E13.19.7"),sQuery(id+"F0.wireOp",EDGE,"E13.19.8"),sQuery(id+"F0.wireOp",EDGE,"E13.19.9"),sQuery(id+"F0.wireOp",EDGE,"E13.19.10"),sQuery(id+"F0.wireOp",EDGE,"E13.19.11"),sQuery(id+"F0.wireOp",EDGE,"E13.20.0"),sQuery(id+"F0.wireOp",EDGE,"E13.20.1"),sQuery(id+"F0.wireOp",EDGE,"E13.20.2"),sQuery(id+"F0.wireOp",EDGE,"E13.20.3"),sQuery(id+"F0.wireOp",EDGE,"E13.20.4"),sQuery(id+"F0.wireOp",EDGE,"E13.20.5"),sQuery(id+"F0.wireOp",EDGE,"E13.20.6"),sQuery(id+"F0.wireOp",EDGE,"E13.20.7"),sQuery(id+"F0.wireOp",EDGE,"E13.20.8"),sQuery(id+"F0.wireOp",EDGE,"E13.20.9"),sQuery(id+"F0.wireOp",EDGE,"E13.20.10"),sQuery(id+"F0.wireOp",EDGE,"E13.20.11"),sQuery(id+"F0.wireOp",EDGE,"E13.21.0"),sQuery(id+"F0.wireOp",EDGE,"E13.21.1"),sQuery(id+"F0.wireOp",EDGE,"E13.21.2"),sQuery(id+"F0.wireOp",EDGE,"E13.21.3"),sQuery(id+"F0.wireOp",EDGE,"E13.21.4"),sQuery(id+"F0.wireOp",EDGE,"E13.21.5"),sQuery(id+"F0.wireOp",EDGE,"E13.21.6"),sQuery(id+"F0.wireOp",EDGE,"E13.21.7"),sQuery(id+"F0.wireOp",EDGE,"E13.21.8"),sQuery(id+"F0.wireOp",EDGE,"E13.21.9"),sQuery(id+"F0.wireOp",EDGE,"E13.21.10"),sQuery(id+"F0.wireOp",EDGE,"E13.21.11"),sQuery(id+"F0.wireOp",EDGE,"E13.22.0"),sQuery(id+"F0.wireOp",EDGE,"E13.22.1"),sQuery(id+"F0.wireOp",EDGE,"E13.22.2"),sQuery(id+"F0.wireOp",EDGE,"E13.22.3"),sQuery(id+"F0.wireOp",EDGE,"E13.22.4"),sQuery(id+"F0.wireOp",EDGE,"E13.22.5"),sQuery(id+"F0.wireOp",EDGE,"E13.22.6"),sQuery(id+"F0.wireOp",EDGE,"E13.22.7"),sQuery(id+"F0.wireOp",EDGE,"E13.22.8"),sQuery(id+"F0.wireOp",EDGE,"E13.22.9"),sQuery(id+"F0.wireOp",EDGE,"E13.22.10"),sQuery(id+"F0.wireOp",EDGE,"E13.22.11"),sQuery(id+"F0.wireOp",EDGE,"E13.23.0"),sQuery(id+"F0.wireOp",EDGE,"E13.23.1"),sQuery(id+"F0.wireOp",EDGE,"E13.23.2"),sQuery(id+"F0.wireOp",EDGE,"E13.23.3"),sQuery(id+"F0.wireOp",EDGE,"E13.23.4"),sQuery(id+"F0.wireOp",EDGE,"E13.23.5"),sQuery(id+"F0.wireOp",EDGE,"E13.23.6"),sQuery(id+"F0.wireOp",EDGE,"E13.23.7"),sQuery(id+"F0.wireOp",EDGE,"E13.23.8"),sQuery(id+"F0.wireOp",EDGE,"E13.23.9"),sQuery(id+"F0.wireOp",EDGE,"E13.23.10"),sQuery(id+"F0.wireOp",EDGE,"E13.23.11"),sQuery(id+"F0.wireOp",EDGE,"E13.24.0"),sQuery(id+"F0.wireOp",EDGE,"E13.24.1"),sQuery(id+"F0.wireOp",EDGE,"E13.24.2"),sQuery(id+"F0.wireOp",EDGE,"E13.24.3"),sQuery(id+"F0.wireOp",EDGE,"E13.24.4"),sQuery(id+"F0.wireOp",EDGE,"E13.24.5"),sQuery(id+"F0.wireOp",EDGE,"E13.24.6"),sQuery(id+"F0.wireOp",EDGE,"E13.24.7"),sQuery(id+"F0.wireOp",EDGE,"E13.24.8"),sQuery(id+"F0.wireOp",EDGE,"E13.24.9"),sQuery(id+"F0.wireOp",EDGE,"E13.24.10"),sQuery(id+"F0.wireOp",EDGE,"E13.24.11"),sQuery(id+"F0.wireOp",EDGE,"E13.25.0"),sQuery(id+"F0.wireOp",EDGE,"E13.25.1"),sQuery(id+"F0.wireOp",EDGE,"E13.25.2"),sQuery(id+"F0.wireOp",EDGE,"E13.25.3"),sQuery(id+"F0.wireOp",EDGE,"E13.25.4"),sQuery(id+"F0.wireOp",EDGE,"E13.25.5"),sQuery(id+"F0.wireOp",EDGE,"E13.25.6"),sQuery(id+"F0.wireOp",EDGE,"E13.25.7"),sQuery(id+"F0.wireOp",EDGE,"E13.25.8"),sQuery(id+"F0.wireOp",EDGE,"E13.25.9"),sQuery(id+"F0.wireOp",EDGE,"E13.25.10"),sQuery(id+"F0.wireOp",EDGE,"E13.25.11"),sQuery(id+"F0.wireOp",EDGE,"E13.26.0"),sQuery(id+"F0.wireOp",EDGE,"E13.26.1"),sQuery(id+"F0.wireOp",EDGE,"E13.26.2"),sQuery(id+"F0.wireOp",EDGE,"E13.26.3"),sQuery(id+"F0.wireOp",EDGE,"E13.26.4"),sQuery(id+"F0.wireOp",EDGE,"E13.26.5"),sQuery(id+"F0.wireOp",EDGE,"E13.26.6"),sQuery(id+"F0.wireOp",EDGE,"E13.26.7"),sQuery(id+"F0.wireOp",EDGE,"E13.26.8"),sQuery(id+"F0.wireOp",EDGE,"E13.26.9"),sQuery(id+"F0.wireOp",EDGE,"E13.26.10"),sQuery(id+"F0.wireOp",EDGE,"E13.26.11"),sQuery(id+"F0.wireOp",EDGE,"E13.27.0"),sQuery(id+"F0.wireOp",EDGE,"E13.27.1"),sQuery(id+"F0.wireOp",EDGE,"E13.27.2"),sQuery(id+"F0.wireOp",EDGE,"E13.27.3"),sQuery(id+"F0.wireOp",EDGE,"E13.27.4"),sQuery(id+"F0.wireOp",EDGE,"E13.27.5"),sQuery(id+"F0.wireOp",EDGE,"E13.27.6"),sQuery(id+"F0.wireOp",EDGE,"E13.27.7"),sQuery(id+"F0.wireOp",EDGE,"E13.27.8"),sQuery(id+"F0.wireOp",EDGE,"E13.27.9"),sQuery(id+"F0.wireOp",EDGE,"E13.27.10"),sQuery(id+"F0.wireOp",EDGE,"E13.27.11"),sQuery(id+"F0.wireOp",EDGE,"E13.28.0"),sQuery(id+"F0.wireOp",EDGE,"E13.28.1"),sQuery(id+"F0.wireOp",EDGE,"E13.28.2"),sQuery(id+"F0.wireOp",EDGE,"E13.28.3"),sQuery(id+"F0.wireOp",EDGE,"E13.28.4"),sQuery(id+"F0.wireOp",EDGE,"E13.28.5"),sQuery(id+"F0.wireOp",EDGE,"E13.28.6"),sQuery(id+"F0.wireOp",EDGE,"E13.28.7"),sQuery(id+"F0.wireOp",EDGE,"E13.28.8"),sQuery(id+"F0.wireOp",EDGE,"E13.28.9"),sQuery(id+"F0.wireOp",EDGE,"E13.28.10"),sQuery(id+"F0.wireOp",EDGE,"E13.28.11"),sQuery(id+"F0.wireOp",EDGE,"E13.29.0"),sQuery(id+"F0.wireOp",EDGE,"E13.29.1"),sQuery(id+"F0.wireOp",EDGE,"E13.29.2"),sQuery(id+"F0.wireOp",EDGE,"E13.29.3"),sQuery(id+"F0.wireOp",EDGE,"E13.29.4"),sQuery(id+"F0.wireOp",EDGE,"E13.29.5"),sQuery(id+"F0.wireOp",EDGE,"E13.29.6"),sQuery(id+"F0.wireOp",EDGE,"E13.29.7"),sQuery(id+"F0.wireOp",EDGE,"E13.29.8"),sQuery(id+"F0.wireOp",EDGE,"E13.29.9"),sQuery(id+"F0.wireOp",EDGE,"E13.29.10"),sQuery(id+"F0.wireOp",EDGE,"E13.29.11"),sQuery(id+"F0.wireOp",EDGE,"E13.30.0"),sQuery(id+"F0.wireOp",EDGE,"E13.30.1"),sQuery(id+"F0.wireOp",EDGE,"E13.30.2"),sQuery(id+"F0.wireOp",EDGE,"E13.30.3"),sQuery(id+"F0.wireOp",EDGE,"E13.30.4"),sQuery(id+"F0.wireOp",EDGE,"E13.30.5"),sQuery(id+"F0.wireOp",EDGE,"E13.30.6"),sQuery(id+"F0.wireOp",EDGE,"E13.30.7"),sQuery(id+"F0.wireOp",EDGE,"E13.30.8"),sQuery(id+"F0.wireOp",EDGE,"E13.30.9"),sQuery(id+"F0.wireOp",EDGE,"E13.30.10"),sQuery(id+"F0.wireOp",EDGE,"E13.30.11"),sQuery(id+"F0.wireOp",EDGE,"E13.31.0"),sQuery(id+"F0.wireOp",EDGE,"E13.31.1"),sQuery(id+"F0.wireOp",EDGE,"E13.31.2"),sQuery(id+"F0.wireOp",EDGE,"E13.31.3"),sQuery(id+"F0.wireOp",EDGE,"E13.31.4"),sQuery(id+"F0.wireOp",EDGE,"E13.31.5"),sQuery(id+"F0.wireOp",EDGE,"E13.31.6"),sQuery(id+"F0.wireOp",EDGE,"E13.31.7"),sQuery(id+"F0.wireOp",EDGE,"E13.31.8"),sQuery(id+"F0.wireOp",EDGE,"E13.31.9"),sQuery(id+"F0.wireOp",EDGE,"E13.31.10"),sQuery(id+"F0.wireOp",EDGE,"E13.31.11"),sQuery(id+"F0.wireOp",EDGE,"E13.32.0"),sQuery(id+"F0.wireOp",EDGE,"E13.32.1"),sQuery(id+"F0.wireOp",EDGE,"E13.32.2"),sQuery(id+"F0.wireOp",EDGE,"E13.32.3"),sQuery(id+"F0.wireOp",EDGE,"E13.32.4"),sQuery(id+"F0.wireOp",EDGE,"E13.32.5"),sQuery(id+"F0.wireOp",EDGE,"E13.32.6"),sQuery(id+"F0.wireOp",EDGE,"E13.32.7"),sQuery(id+"F0.wireOp",EDGE,"E13.32.8"),sQuery(id+"F0.wireOp",EDGE,"E13.32.9"),sQuery(id+"F0.wireOp",EDGE,"E13.32.10"),sQuery(id+"F0.wireOp",EDGE,"E13.32.11"),sQuery(id+"F0.wireOp",EDGE,"E13.33.0"),sQuery(id+"F0.wireOp",EDGE,"E13.33.1"),sQuery(id+"F0.wireOp",EDGE,"E13.33.2"),sQuery(id+"F0.wireOp",EDGE,"E13.33.3"),sQuery(id+"F0.wireOp",EDGE,"E13.33.4"),sQuery(id+"F0.wireOp",EDGE,"E13.33.5"),sQuery(id+"F0.wireOp",EDGE,"E13.33.6"),sQuery(id+"F0.wireOp",EDGE,"E13.33.7"),sQuery(id+"F0.wireOp",EDGE,"E13.33.8"),sQuery(id+"F0.wireOp",EDGE,"E13.33.9"),sQuery(id+"F0.wireOp",EDGE,"E13.33.10"),sQuery(id+"F0.wireOp",EDGE,"E13.33.11"),sQuery(id+"F0.wireOp",EDGE,"E13.34.0"),sQuery(id+"F0.wireOp",EDGE,"E13.34.1"),sQuery(id+"F0.wireOp",EDGE,"E13.34.2"),sQuery(id+"F0.wireOp",EDGE,"E13.34.3"),sQuery(id+"F0.wireOp",EDGE,"E13.34.4"),sQuery(id+"F0.wireOp",EDGE,"E13.34.5"),sQuery(id+"F0.wireOp",EDGE,"E13.34.6"),sQuery(id+"F0.wireOp",EDGE,"E13.34.7"),sQuery(id+"F0.wireOp",EDGE,"E13.34.8"),sQuery(id+"F0.wireOp",EDGE,"E13.34.9"),sQuery(id+"F0.wireOp",EDGE,"E13.34.10"),sQuery(id+"F0.wireOp",EDGE,"E13.34.11"),sQuery(id+"F0.wireOp",EDGE,"E13.35.0"),sQuery(id+"F0.wireOp",EDGE,"E13.35.1"),sQuery(id+"F0.wireOp",EDGE,"E13.35.2"),sQuery(id+"F0.wireOp",EDGE,"E13.35.3"),sQuery(id+"F0.wireOp",EDGE,"E13.35.4"),sQuery(id+"F0.wireOp",EDGE,"E13.35.5"),sQuery(id+"F0.wireOp",EDGE,"E13.35.6"),sQuery(id+"F0.wireOp",EDGE,"E13.35.7"),sQuery(id+"F0.wireOp",EDGE,"E13.35.8"),sQuery(id+"F0.wireOp",EDGE,"E13.35.9"),sQuery(id+"F0.wireOp",EDGE,"E13.35.10"),sQuery(id+"F0.wireOp",EDGE,"E13.35.11"),sQuery(id+"F0.wireOp",EDGE,"E14.trimOffspring"),sQuery(id+"F0.wireOp",EDGE,"E15.trimOffspring"),sQuery(id+"F0.wireOp",EDGE,"E16.trimOffspring"),sQuery(id+"F0.wireOp",EDGE,"E17.trimOffspring"),sQuery(id+"F0.wireOp",EDGE,"E18.trimOffspring"),sQuery(id+"F0.wireOp",EDGE,"E19.trimOffspring"),sQuery(id+"F0.wireOp",EDGE,"E20.trimOffspring"),sQuery(id+"F0.wireOp",EDGE,"E21.trimOffspring"),sQuery(id+"F0.wireOp",EDGE,"E22.trimOffspring"),sQuery(id+"F0.wireOp",EDGE,"E23.trimOffspring"),sQuery(id+"F0.wireOp",EDGE,"E24.trimOffspring"),sQuery(id+"F0.wireOp",EDGE,"E25.trimOffspring"),sQuery(id+"F0.wireOp",EDGE,"E26.trimOffspring"),sQuery(id+"F0.wireOp",EDGE,"E27.trimOffspring"),sQuery(id+"F0.wireOp",EDGE,"E28.trimOffspring"),sQuery(id+"F0.wireOp",EDGE,"E29.trimOffspring"),sQuery(id+"F0.wireOp",EDGE,"E30.trimOffspring"),sQuery(id+"F0.wireOp",EDGE,"E31.trimOffspring"),sQuery(id+"F0.wireOp",EDGE,"E32.trimOffspring"),sQuery(id+"F0.wireOp",EDGE,"E33.trimOffspring"),sQuery(id+"F0.wireOp",EDGE,"E34.trimOffspring"),sQuery(id+"F0.wireOp",EDGE,"E35.trimOffspring"),sQuery(id+"F0.wireOp",EDGE,"E36.trimOffspring"),sQuery(id+"F0.wireOp",EDGE,"E37.trimOffspring"),sQuery(id+"F0.wireOp",EDGE,"E38.trimOffspring"),sQuery(id+"F0.wireOp",EDGE,"E39.trimOffspring"),sQuery(id+"F0.wireOp",EDGE,"E40.trimOffspring"),sQuery(id+"F0.wireOp",EDGE,"E41.trimOffspring"),sQuery(id+"F0.wireOp",EDGE,"E42.trimOffspring"),sQuery(id+"F0.wireOp",EDGE,"E43.trimOffspring"),sQuery(id+"F0.wireOp",EDGE,"E44.trimOffspring"),sQuery(id+"F0.wireOp",EDGE,"E45.trimOffspring"),sQuery(id+"F0.wireOp",EDGE,"E46.trimOffspring"),sQuery(id+"F0.wireOp",EDGE,"E47"),sQuery(id+"F0.wireOp",EDGE,"E48"),sQuery(id+"F0.wireOp",EDGE,"E49")])],"isStart":false});
            shell(context, id + "F4", {"entities" : qUnion([Q0]), "thickness" : 6.35 * mm});
        }
        {
            var Q0;
            Q0=qCreatedBy(makeId("Right.planeOp"),FACE);
            cPlane(context, id + "F5", {"entities" : qUnion([Q0]), "cplaneType" : CPlaneType.OFFSET, "offset" : 9.52 * mm, "width" : 152.4 * mm, "height" : 152.4 * mm});
        }
        {
            var Q0;
            Q0=qCreatedBy(id+"F5.planeOp",FACE);
            var sketch = newSketch(context, id + "F6", { "sketchPlane" : qUnion([Q0])});
            skCircle(sketch, "E51", {"center": v(-9.53, 0) * mm, "radius": 0.91 * mm});
            skSolve(sketch);
        }
        {
            var Q0;
            Q0=makeQuery(id+"F6.imprint","IMPRINT",FACE,{"disambiguationData":[TD([[makeQuery(id+"F6.imprint","IMPRINT",EDGE,{"derivedFrom":sQuery(id+"F6.wireOp",EDGE,"E51")}),1.0]])]});
            extrude(context, id + "F7", {"entities" : qUnion([Q0]), "operationType" : NewBodyOperationType.REMOVE, "oppositeDirection" : true, "depth" : 9.52 * mm});
        }
    });
